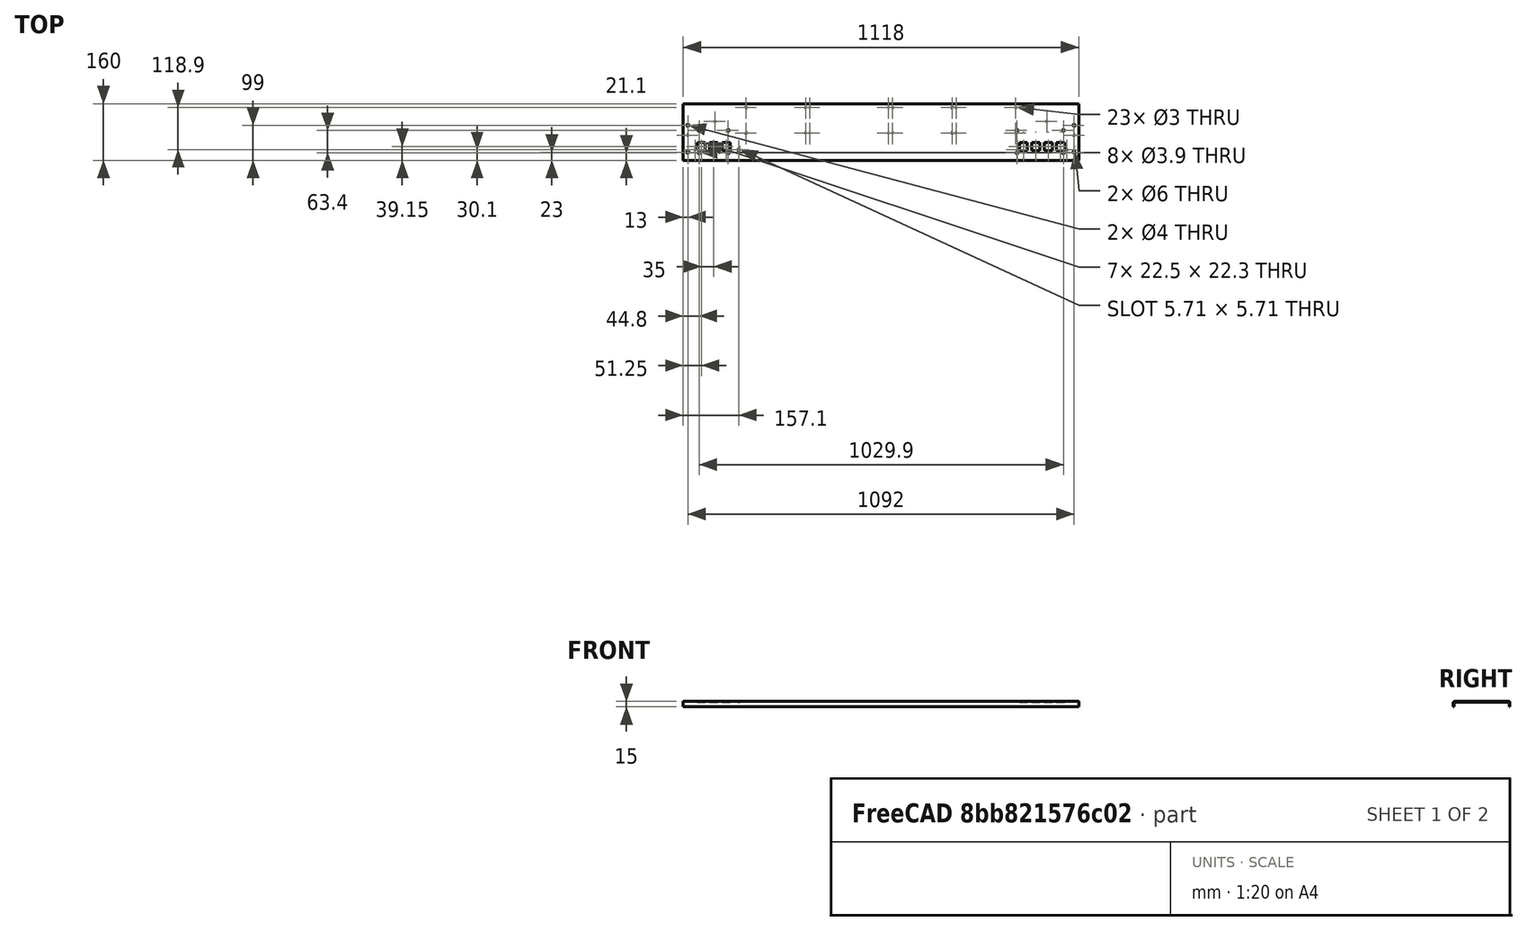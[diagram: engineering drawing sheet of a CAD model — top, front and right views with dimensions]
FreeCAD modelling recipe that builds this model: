
FCSTD DOCUMENT  (FreeCAD 0.20R29603 (Git))
Label: PanneauCommandeSupportTirettes
License: All rights reserved
LicenseURL: http://en.wikipedia.org/wiki/All_rights_reserved
objects: TechDraw::DrawViewDimension×108, TechDraw::DrawViewBalloon×27, Sketcher::SketchObject×10, TechDraw::DrawSVGTemplate×8, TechDraw::DrawViewPart×8, TechDraw::DrawPage×8, PartDesign::Pocket×7, TechDraw::DrawViewAnnotation×7, TechDraw::DrawRichAnno×5, TechDraw::DrawProjGroupItem×3, PartDesign::LinearPattern×2, PartDesign::FeaturePython×2, PartDesign::Hole×2, PartDesign::Pad×1, TechDraw::DrawProjGroup×1, PartDesign::Body×1
note: 35 computed .brp shape members not serialized (recipe doc carries the construction recipe); baked Part::Feature solids carry a one-line shape summary decoded from their .brp

FEATURE [Sketcher::SketchObject] Sketch
  FullyConstrained = true
  MapMode = 5
  Support = -> [XY_Plane]
  sketch-geometry (4):
    g0: LineSegment StartX=0 StartY=0 StartZ=0 EndX=1118 EndY=0 EndZ=0
    g1: LineSegment StartX=1118 StartY=0 StartZ=0 EndX=1118 EndY=154 EndZ=0
    g2: LineSegment StartX=1118 StartY=154 StartZ=0 EndX=0 EndY=154 EndZ=0
    g3: LineSegment StartX=0 StartY=154 StartZ=0 EndX=0 EndY=0 EndZ=0
  constraints (11):
    c: Coincident(g0,g1)
    c: Coincident(g1,g2)
    c: Coincident(g2,g3)
    c: Coincident(g3,g0)
    c: Horizontal(g0)
    c: Horizontal(g2)
    c: Vertical(g1)
    c: Vertical(g3)
    c: Coincident(g0,g-1)
    c: DistanceX(g2,g2) = 1118
    c: DistanceY(g3,g3) = 154
FEATURE [PartDesign::Pad] Pad
  Direction = (0,0,1)
  Length = 2
  Length2 = 10
  Profile = -> Sketch
  ReferenceAxis = -> Sketch [N_Axis]
  Reversed = true
  Type = 0
FEATURE [Sketcher::SketchObject] Sketch001  label="PercageGauche"
  FullyConstrained = true
  MapMode = 5
  Support = -> [XY_Plane]
  sketch-geometry (4):
    g0: LineSegment StartX=40 StartY=47.3 StartZ=0 EndX=62.5 EndY=47.3 EndZ=0
    g1: LineSegment StartX=62.5 StartY=47.3 StartZ=0 EndX=62.5 EndY=25 EndZ=0
    g2: LineSegment StartX=62.5 StartY=25 StartZ=0 EndX=40 EndY=25 EndZ=0
    g3: LineSegment StartX=40 StartY=25 StartZ=0 EndX=40 EndY=47.3 EndZ=0
  constraints (12):
    c: Coincident(g0,g1)
    c: Coincident(g1,g2)
    c: Coincident(g2,g3)
    c: Coincident(g3,g0)
    c: Horizontal(g0)
    c: Horizontal(g2)
    c: Vertical(g1)
    c: Vertical(g3)
    c: DistanceX(g2,g2) = 22.5
    c: DistanceY(g1,g1) = 22.3
    c: DistanceX(g-1,g0) = 40
    c: DistanceY(g-1,g2) = 25
FEATURE [PartDesign::Pocket] Pocket  label="PercageGauche001"
  BaseFeature = -> Pad
  Direction = (0,0,-1)
  Length = 5
  Length2 = 5
  Profile = -> Sketch001
  ReferenceAxis = -> Sketch001 [N_Axis]
  Type = 1
FEATURE [PartDesign::LinearPattern] LinearPattern
  BaseFeature = -> Pocket
  Direction = -> Sketch001 [H_Axis]
  Length = 70
  Occurrences = 3
  Originals = -> [Pocket]
FEATURE [Sketcher::SketchObject] Sketch002  label="PercageDroite"
  ExternalGeometry = -> [LinearPattern]
  FullyConstrained = true
  MapMode = 5
  Support = -> [XY_Plane]
  sketch-geometry (4):
    g0: LineSegment StartX=1055.5 StartY=47.3 StartZ=0 EndX=1078 EndY=47.3 EndZ=0
    g1: LineSegment StartX=1078 StartY=47.3 StartZ=0 EndX=1078 EndY=25 EndZ=0
    g2: LineSegment StartX=1078 StartY=25 StartZ=0 EndX=1055.5 EndY=25 EndZ=0
    g3: LineSegment StartX=1055.5 StartY=25 StartZ=0 EndX=1055.5 EndY=47.3 EndZ=0
  constraints (12):
    c: Coincident(g0,g1)
    c: Coincident(g1,g2)
    c: Coincident(g2,g3)
    c: Coincident(g3,g0)
    c: Horizontal(g0)
    c: Horizontal(g2)
    c: Vertical(g1)
    c: Vertical(g3)
    c: DistanceY(g1,g1) = 22.3
    c: DistanceX(g0,g0) = 22.5
    c: DistanceY(g-1,g2) = 25
    c: DistanceX(g-3,g1) = -40
FEATURE [PartDesign::Pocket] Pocket001  label="PercageDroite001"
  BaseFeature = -> LinearPattern
  Direction = (0,0,-1)
  Length = 5
  Length2 = 5
  Profile = -> Sketch002
  ReferenceAxis = -> Sketch002 [N_Axis]
  Type = 1
FEATURE [PartDesign::LinearPattern] LinearPattern001
  BaseFeature = -> Pocket001
  Direction = -> Sketch002 [H_Axis]
  Length = 105
  Occurrences = 4
  Originals = -> [Pocket001]
  Reversed = true
FEATURE [PartDesign::FeaturePython] Bend  # WARN: FeaturePython — macro-defined, semantics opaque (R4)
  AutoMiter = true
  BaseFeature = -> LinearPattern001
  BendType = 0
  LengthList = [12]
  LengthSpec = 0
  ReliefFactor = 0.7
  UseReliefFactor = false
  angle = 90
  baseObject = -> LinearPattern001 [Face1]
  bendAList = [90]
  extend1 = 0
  extend2 = 0
  gap1 = 0
  gap2 = 0
  invert = false
  kfactor = 0.5
  length = 12
  maxExtendDist = 5
  minGap = 0.1
  minReliefGap = 1
  miterangle1 = 0
  miterangle2 = 0
  offset = 0
  radius = 1
  reliefType = 0
  reliefd = 1
  reliefw = 0.8
  sketchflip = false
  sketchinvert = false
  unfold = false
FEATURE [PartDesign::FeaturePython] Bend001  # WARN: FeaturePython — macro-defined, semantics opaque (R4)
  AutoMiter = true
  BaseFeature = -> Bend
  BendType = 0
  LengthList = [12]
  LengthSpec = 0
  ReliefFactor = 0.7
  UseReliefFactor = false
  angle = 90
  baseObject = -> Bend [Face13]
  bendAList = [90]
  extend1 = 0
  extend2 = 0
  gap1 = 0
  gap2 = 0
  invert = false
  kfactor = 0.5
  length = 12
  maxExtendDist = 5
  minGap = 0.1
  minReliefGap = 1
  miterangle1 = 0
  miterangle2 = 0
  offset = 0
  radius = 1
  reliefType = 0
  reliefd = 1
  reliefw = 0.8
  sketchflip = false
  sketchinvert = false
  unfold = false
FEATURE [TechDraw::DrawSVGTemplate] Template
  Height = 210
  Orientation = 1
  Width = 297
FEATURE [TechDraw::DrawProjGroupItem] ProjItem  label="Front"
  CoarseView = false
  Direction = (0,0,1)
  Focus = 100
  HardHidden = false
  IsoCount = 0
  IsoHidden = false
  IsoVisible = false
  LockPosition = true
  Perspective = false
  Rotation = 0
  RotationVector = (1,0,0)
  Scale = 0.2
  ScaleType = 2
  SeamHidden = false
  SeamVisible = true
  SmoothHidden = false
  SmoothVisible = true
  Source = -> [Bend001]
  Type = 0
  X = 0
  XDirection = (1,0,0)
  Y = 0
FEATURE [TechDraw::DrawProjGroupItem] ProjItem001  label="Bottom"
  CoarseView = false
  Direction = (0,-1,0)
  Focus = 100
  HardHidden = false
  IsoCount = 0
  IsoHidden = false
  IsoVisible = false
  LockPosition = false
  Perspective = false
  Rotation = 0
  RotationVector = (1,0,0)
  ScaleType = 2
  SeamHidden = false
  SeamVisible = true
  SmoothHidden = false
  SmoothVisible = true
  Source = -> [Bend001]
  Type = 5
  X = 0
  XDirection = (1,0,0)
  Y = 47
FEATURE [TechDraw::DrawProjGroupItem] ProjItem002  label="Right"
  CoarseView = false
  Direction = (1,0,1e-16)
  Focus = 100
  HardHidden = false
  IsoCount = 0
  IsoHidden = false
  IsoVisible = false
  LockPosition = false
  Perspective = false
  Rotation = 0
  RotationVector = (1,0,0)
  ScaleType = 2
  SeamHidden = false
  SeamVisible = true
  SmoothHidden = false
  SmoothVisible = true
  Source = -> [Bend001]
  Type = 2
  X = -152.058
  XDirection = (1e-16,0,-1)
  Y = 0
FEATURE [TechDraw::DrawProjGroup] ProjGroup
  Anchor = -> ProjItem
  AutoDistribute = false
  LockPosition = false
  ProjectionType = 0
  Rotation = 0
  Scale = 0.2
  ScaleType = 2
  Source = -> [Bend001]
  Views = -> [ProjItem,ProjItem001,ProjItem002]
  X = 172.705
  Y = 99.0316
  spacingX = 15
  spacingY = 15
FEATURE [TechDraw::DrawViewDimension] Dimension
  AngleOverride = false
  Arbitrary = false
  ArbitraryTolerances = false
  EqualTolerance = true
  ExtensionAngle = 0
  FormatSpec = %.2w
  FormatSpecOverTolerance = %+.2w
  FormatSpecUnderTolerance = %+.2w
  Inverted = false
  LineAngle = 0
  LockPosition = false
  MeasureType = 1
  OverTolerance = 0
  References2D = -> [ProjItem]
  Rotation = 0
  ScaleType = 0
  TheoreticalExact = false
  Type = 1
  UnderTolerance = 0
  X = 2.98421
  Y = -48.3158
FEATURE [TechDraw::DrawViewDimension] Dimension001
  AngleOverride = false
  Arbitrary = false
  ArbitraryTolerances = false
  EqualTolerance = true
  ExtensionAngle = 0
  FormatSpec = %.2w
  FormatSpecOverTolerance = %+.2w
  FormatSpecUnderTolerance = %+.2w
  Inverted = false
  LineAngle = 0
  LockPosition = false
  MeasureType = 1
  OverTolerance = 0
  References2D = -> [ProjItem]
  Rotation = 0
  ScaleType = 0
  TheoreticalExact = false
  Type = 2
  UnderTolerance = 0
  X = -126.143
  Y = 3.14776
FEATURE [TechDraw::DrawViewBalloon] Balloon
  BubbleShape = 0
  EndType = 0
  EndTypeScale = 1
  KinkLength = 5
  LockPosition = false
  OriginX = -215.581
  OriginY = -7.47892
  Rotation = 0
  ScaleType = 0
  ShapeScale = 1
  SourceView = -> ProjItem
  Text = 1
  TextWrapLen = -1
  X = -91.4035
  Y = 121.304
FEATURE [TechDraw::DrawViewBalloon] Balloon001
  BubbleShape = 0
  EndType = 0
  EndTypeScale = 1
  KinkLength = 5
  LockPosition = false
  OriginX = -5.49057
  OriginY = 0
  Rotation = 0
  ScaleType = 0
  ShapeScale = 1
  SourceView = -> ProjItem002
  Text = 2
  TextWrapLen = -1
  X = 94.5094
  Y = 100
FEATURE [TechDraw::DrawRichAnno] RichTextAnnotation
  AnnoText = <!DOCTYPE HTML PUBLIC "-//W3C//DTD HTML 4.0//EN" "http://www.w3.org/TR/REC-html40/strict.dtd">\n<html><head><meta name="qrichtext" content="1" /><style type="text/css">\np, li { white-space: pre-wrap; }\n</style></head><body style=" font-family:'osifont'; font-size:9pt; font-weight:400; font-style:normal;">\n<p style=" margin-top:0px; margin-bottom:0px; margin-left:0px; margin-right:0px; -qt-block-indent:0; text-indent:0px;"><span style=" font-family:'Sans Serif'; font-size:10pt;">1 : vue de dessus</span></p>\n<p style=" margin-top:0px; margin-bottom:0px; margin-left:0px; margin-right:0px; -qt-block-indent:0; text-indent:0px;"><span style=" font-family:'Sans Serif'; font-size:10pt;">2 : dessous de la pièce</span></p></body></html>
  LockPosition = false
  MaxWidth = -1
  Rotation = 0
  ScaleType = 0
  ShowFrame = false
  X = 55.4737
  Y = 20.7237
FEATURE [TechDraw::DrawSVGTemplate] Template001
  Height = 210
  Orientation = 1
  Width = 297
FEATURE [TechDraw::DrawViewPart] View001
  CoarseView = false
  Direction = (1,0,0)
  Focus = 100
  HardHidden = false
  IsoCount = 0
  IsoHidden = false
  IsoVisible = false
  LockPosition = false
  Perspective = false
  Rotation = 90
  ScaleType = 2
  SeamHidden = false
  SeamVisible = true
  SmoothHidden = false
  SmoothVisible = true
  Source = -> [Bend001]
  X = 148.5
  XDirection = (1,0,0)
  Y = 105
FEATURE [TechDraw::DrawViewDimension] Dimension002
  AngleOverride = false
  Arbitrary = false
  ArbitraryTolerances = false
  EqualTolerance = true
  ExtensionAngle = 0
  FormatSpec = %.2w
  FormatSpecOverTolerance = %+.2w
  FormatSpecUnderTolerance = %+.2w
  Inverted = false
  LineAngle = 0
  LockPosition = false
  MeasureType = 1
  OverTolerance = 0
  References2D = -> [View001]
  Rotation = 0
  ScaleType = 0
  TheoreticalExact = false
  Type = 1
  UnderTolerance = 0
  X = 0.257011
  Y = 40.0608
FEATURE [TechDraw::DrawViewDimension] Dimension003
  AngleOverride = false
  Arbitrary = false
  ArbitraryTolerances = false
  EqualTolerance = true
  ExtensionAngle = 0
  FormatSpec = %.2w
  FormatSpecOverTolerance = %+.2w
  FormatSpecUnderTolerance = %+.2w
  Inverted = false
  LineAngle = 0
  LockPosition = false
  MeasureType = 1
  OverTolerance = 0
  References2D = -> [View001]
  Rotation = 0
  ScaleType = 0
  TheoreticalExact = false
  Type = 1
  UnderTolerance = 0
  X = -0.514022
  Y = 59.6778
FEATURE [TechDraw::DrawViewDimension] Dimension004
  AngleOverride = false
  Arbitrary = false
  ArbitraryTolerances = false
  EqualTolerance = true
  ExtensionAngle = 0
  FormatSpec = %.2w
  FormatSpecOverTolerance = %+.2w
  FormatSpecUnderTolerance = %+.2w
  Inverted = false
  LineAngle = 0
  LockPosition = false
  MeasureType = 1
  OverTolerance = 0
  References2D = -> [View001]
  Rotation = 0
  ScaleType = 0
  TheoreticalExact = false
  Type = 2
  UnderTolerance = 0
  X = -112.168
  Y = -14.9862
FEATURE [TechDraw::DrawViewBalloon] Balloon002
  BubbleShape = 0
  EndType = 0
  EndTypeScale = 1
  KinkLength = 5
  LockPosition = false
  OriginX = -2.27e-14
  OriginY = 5.49057
  Rotation = 0
  ScaleType = 0
  ShapeScale = 1
  SourceView = -> View001
  Text = 1
  TextWrapLen = -1
  X = 25
  Y = -25
FEATURE [TechDraw::DrawRichAnno] RichTextAnnotation001
  AnnoText = <!DOCTYPE HTML PUBLIC "-//W3C//DTD HTML 4.0//EN" "http://www.w3.org/TR/REC-html40/strict.dtd">\n<html><head><meta name="qrichtext" content="1" /><style type="text/css">\np, li { white-space: pre-wrap; }\n</style></head><body style=" font-family:'Sans Serif'; font-size:9pt; font-weight:400; font-style:normal;">\n<p style=" margin-top:0px; margin-bottom:0px; margin-left:0px; margin-right:0px; -qt-block-indent:0; text-indent:0px;"><span style=" font-size:10pt;">1 : dessous de la pièce</span></p></body></html>
  LockPosition = false
  MaxWidth = -1
  Rotation = 0
  ScaleType = 0
  ShowFrame = false
  X = 91.5
  Y = 44
FEATURE [TechDraw::DrawViewDimension] Dimension005
  AngleOverride = false
  Arbitrary = false
  ArbitraryTolerances = false
  EqualTolerance = true
  ExtensionAngle = 0
  FormatSpec = %.2w
  FormatSpecOverTolerance = %+.2w
  FormatSpecUnderTolerance = %+.2w
  Inverted = false
  LineAngle = 0
  LockPosition = false
  MeasureType = 1
  OverTolerance = 0
  References2D = -> [View001]
  Rotation = 0
  ScaleType = 0
  TheoreticalExact = false
  Type = 2
  UnderTolerance = 0
  X = 99.7898
  Y = -15.7151
FEATURE [TechDraw::DrawPage] Page001  label="vue-de-cote"
  KeepUpdated = true
  NextBalloonIndex = 2
  ProjectionType = 0
  Template = -> Template001
  Views = -> [View001,Dimension002,Dimension003,Dimension004,Balloon002,RichTextAnnotation001,Dimension005]
FEATURE [TechDraw::DrawSVGTemplate] Template002
  Height = 210
  Orientation = 1
  Width = 297
FEATURE [TechDraw::DrawViewPart] View
  CoarseView = false
  Direction = (0,0,1)
  Focus = 100
  HardHidden = false
  IsoCount = 0
  IsoHidden = false
  IsoVisible = false
  LockPosition = false
  Perspective = false
  Rotation = 0
  Scale = 0.5
  ScaleType = 2
  SeamHidden = false
  SeamVisible = true
  SmoothHidden = false
  SmoothVisible = false
  Source = -> [Bend001]
  X = 301.855
  XDirection = (1,0,0)
  Y = 156.671
FEATURE [TechDraw::DrawViewPart] View002
  CoarseView = false
  Direction = (0,0,1)
  Focus = 100
  HardHidden = false
  IsoCount = 0
  IsoHidden = false
  IsoVisible = false
  LockPosition = false
  Perspective = false
  Rotation = 0
  Scale = 0.5
  ScaleType = 2
  SeamHidden = false
  SeamVisible = true
  SmoothHidden = false
  SmoothVisible = false
  Source = -> [Bend001]
  X = -2.92105
  XDirection = (1,0,0)
  Y = 57.4737
FEATURE [TechDraw::DrawViewDimension] Dimension006
  AngleOverride = false
  Arbitrary = false
  ArbitraryTolerances = false
  EqualTolerance = true
  ExtensionAngle = 0
  FormatSpec = %.2w
  FormatSpecOverTolerance = %+.2w
  FormatSpecUnderTolerance = %+.2w
  Inverted = false
  LineAngle = 0
  LockPosition = false
  MeasureType = 1
  OverTolerance = 0
  References2D = -> [View]
  Rotation = 0
  ScaleType = 0
  TheoreticalExact = false
  Type = 1
  UnderTolerance = 0
  X = -268.36
  Y = 20.4992
FEATURE [TechDraw::DrawViewDimension] Dimension007
  AngleOverride = false
  Arbitrary = false
  ArbitraryTolerances = false
  EqualTolerance = true
  ExtensionAngle = 0
  FormatSpec = %.2w
  FormatSpecOverTolerance = %+.2w
  FormatSpecUnderTolerance = %+.2w
  Inverted = false
  LineAngle = 0
  LockPosition = false
  MeasureType = 1
  OverTolerance = 0
  References2D = -> [View]
  Rotation = 0
  ScaleType = 0
  TheoreticalExact = false
  Type = 1
  UnderTolerance = 0
  X = -236.467
  Y = 34.6237
FEATURE [TechDraw::DrawViewDimension] Dimension008
  AngleOverride = false
  Arbitrary = false
  ArbitraryTolerances = false
  EqualTolerance = true
  ExtensionAngle = 0
  FormatSpec = %.2w
  FormatSpecOverTolerance = %+.2w
  FormatSpecUnderTolerance = %+.2w
  Inverted = false
  LineAngle = 0
  LockPosition = false
  MeasureType = 1
  OverTolerance = 0
  References2D = -> [View]
  Rotation = 0
  ScaleType = 0
  TheoreticalExact = false
  Type = 1
  UnderTolerance = 0
  X = -217.586
  Y = 24.6763
FEATURE [TechDraw::DrawViewDimension] Dimension009
  AngleOverride = false
  Arbitrary = false
  ArbitraryTolerances = false
  EqualTolerance = true
  ExtensionAngle = 0
  FormatSpec = %.2w
  FormatSpecOverTolerance = %+.2w
  FormatSpecUnderTolerance = %+.2w
  Inverted = false
  LineAngle = 0
  LockPosition = false
  MeasureType = 1
  OverTolerance = 0
  References2D = -> [View]
  Rotation = 0
  ScaleType = 0
  TheoreticalExact = false
  Type = 1
  UnderTolerance = 0
  X = -199.257
  Y = 14.4526
FEATURE [TechDraw::DrawViewDimension] Dimension010
  AngleOverride = false
  Arbitrary = false
  ArbitraryTolerances = false
  EqualTolerance = true
  ExtensionAngle = 0
  FormatSpec = %.2w
  FormatSpecOverTolerance = %+.2w
  FormatSpecUnderTolerance = %+.2w
  Inverted = false
  LineAngle = 0
  LockPosition = false
  MeasureType = 1
  OverTolerance = 0
  References2D = -> [View]
  Rotation = 0
  ScaleType = 0
  TheoreticalExact = false
  Type = 2
  UnderTolerance = 0
  X = -185.066
  Y = 0.864474
FEATURE [TechDraw::DrawViewDimension] Dimension011
  AngleOverride = false
  Arbitrary = false
  ArbitraryTolerances = false
  EqualTolerance = true
  ExtensionAngle = 0
  FormatSpec = %.2w
  FormatSpecOverTolerance = %+.2w
  FormatSpecUnderTolerance = %+.2w
  Inverted = false
  LineAngle = 0
  LockPosition = false
  MeasureType = 1
  OverTolerance = 0
  References2D = -> [View]
  Rotation = 0
  ScaleType = 0
  TheoreticalExact = false
  Type = 2
  UnderTolerance = 0
  X = -168.395
  Y = -11.7895
FEATURE [TechDraw::DrawViewDimension] Dimension012
  AngleOverride = false
  Arbitrary = false
  ArbitraryTolerances = false
  EqualTolerance = true
  ExtensionAngle = 0
  FormatSpec = %.2w
  FormatSpecOverTolerance = %+.2w
  FormatSpecUnderTolerance = %+.2w
  Inverted = false
  LineAngle = 0
  LockPosition = false
  MeasureType = 1
  OverTolerance = 0
  References2D = -> [View]
  Rotation = 0
  ScaleType = 0
  TheoreticalExact = false
  Type = 2
  UnderTolerance = 0
  X = -152.737
  Y = -11.4342
FEATURE [TechDraw::DrawViewDimension] Dimension013
  AngleOverride = false
  Arbitrary = false
  ArbitraryTolerances = false
  EqualTolerance = true
  ExtensionAngle = 0
  FormatSpec = %.2w
  FormatSpecOverTolerance = %+.2w
  FormatSpecUnderTolerance = %+.2w
  Inverted = false
  LineAngle = 0
  LockPosition = false
  MeasureType = 1
  OverTolerance = 0
  References2D = -> [View]
  Rotation = 0
  ScaleType = 0
  TheoreticalExact = false
  Type = 1
  UnderTolerance = 0
  X = -267.714
  Y = -3.02507
FEATURE [TechDraw::DrawViewDimension] Dimension014
  AngleOverride = false
  Arbitrary = false
  ArbitraryTolerances = false
  EqualTolerance = true
  ExtensionAngle = 0
  FormatSpec = %.2w
  FormatSpecOverTolerance = %+.2w
  FormatSpecUnderTolerance = %+.2w
  Inverted = false
  LineAngle = 0
  LockPosition = false
  MeasureType = 1
  OverTolerance = 0
  References2D = -> [View]
  Rotation = 0
  ScaleType = 0
  TheoreticalExact = false
  Type = 1
  UnderTolerance = 0
  X = -203.309
  Y = 3.67632
FEATURE [TechDraw::DrawViewDimension] Dimension015
  AngleOverride = false
  Arbitrary = false
  ArbitraryTolerances = false
  EqualTolerance = true
  ExtensionAngle = 0
  FormatSpec = %.2w
  FormatSpecOverTolerance = %+.2w
  FormatSpecUnderTolerance = %+.2w
  Inverted = false
  LineAngle = 0
  LockPosition = false
  MeasureType = 1
  OverTolerance = 0
  References2D = -> [View002]
  Rotation = 0
  ScaleType = 0
  TheoreticalExact = false
  Type = 1
  UnderTolerance = 0
  X = 269.224
  Y = 8.37368
FEATURE [TechDraw::DrawViewDimension] Dimension016
  AngleOverride = false
  Arbitrary = false
  ArbitraryTolerances = false
  EqualTolerance = true
  ExtensionAngle = 0
  FormatSpec = %.2w
  FormatSpecOverTolerance = %+.2w
  FormatSpecUnderTolerance = %+.2w
  Inverted = false
  LineAngle = 0
  LockPosition = false
  MeasureType = 1
  OverTolerance = 0
  References2D = -> [View002]
  Rotation = 0
  ScaleType = 0
  TheoreticalExact = false
  Type = 2
  UnderTolerance = 0
  X = 264.75
  Y = -16.6934
FEATURE [TechDraw::DrawViewDimension] Dimension017
  AngleOverride = false
  Arbitrary = false
  ArbitraryTolerances = false
  EqualTolerance = true
  ExtensionAngle = 0
  FormatSpec = %.2w
  FormatSpecOverTolerance = %+.2w
  FormatSpecUnderTolerance = %+.2w
  Inverted = false
  LineAngle = 0
  LockPosition = false
  MeasureType = 1
  OverTolerance = 0
  References2D = -> [View002]
  Rotation = 0
  ScaleType = 0
  TheoreticalExact = false
  Type = 2
  UnderTolerance = 0
  X = 273.03
  Y = -16.9251
FEATURE [TechDraw::DrawViewDimension] Dimension018
  AngleOverride = false
  Arbitrary = false
  ArbitraryTolerances = false
  EqualTolerance = true
  ExtensionAngle = 0
  FormatSpec = %.2w
  FormatSpecOverTolerance = %+.2w
  FormatSpecUnderTolerance = %+.2w
  Inverted = false
  LineAngle = 0
  LockPosition = false
  MeasureType = 1
  OverTolerance = 0
  References2D = -> [View002]
  Rotation = 0
  ScaleType = 0
  TheoreticalExact = false
  Type = 1
  UnderTolerance = 0
  X = 185.217
  Y = 0.390089
FEATURE [TechDraw::DrawViewDimension] Dimension019
  AngleOverride = false
  Arbitrary = false
  ArbitraryTolerances = false
  EqualTolerance = true
  ExtensionAngle = 0
  FormatSpec = %.2w
  FormatSpecOverTolerance = %+.2w
  FormatSpecUnderTolerance = %+.2w
  Inverted = false
  LineAngle = 0
  LockPosition = false
  MeasureType = 1
  OverTolerance = 0
  References2D = -> [View002]
  Rotation = 0
  ScaleType = 0
  TheoreticalExact = false
  Type = 1
  UnderTolerance = 0
  X = 201.785
  Y = 9.40137
FEATURE [TechDraw::DrawViewDimension] Dimension020
  AngleOverride = false
  Arbitrary = false
  ArbitraryTolerances = false
  EqualTolerance = true
  ExtensionAngle = 0
  FormatSpec = %.2w
  FormatSpecOverTolerance = %+.2w
  FormatSpecUnderTolerance = %+.2w
  Inverted = false
  LineAngle = 0
  LockPosition = false
  MeasureType = 1
  OverTolerance = 0
  References2D = -> [View002]
  Rotation = 0
  ScaleType = 0
  TheoreticalExact = false
  Type = 1
  UnderTolerance = 0
  X = 218.352
  Y = 19.6556
FEATURE [TechDraw::DrawViewDimension] Dimension021
  AngleOverride = false
  Arbitrary = false
  ArbitraryTolerances = false
  EqualTolerance = true
  ExtensionAngle = 0
  FormatSpec = %.2w
  FormatSpecOverTolerance = %+.2w
  FormatSpecUnderTolerance = %+.2w
  Inverted = false
  LineAngle = 0
  LockPosition = false
  MeasureType = 1
  OverTolerance = 0
  References2D = -> [View002]
  Rotation = 0
  ScaleType = 0
  TheoreticalExact = false
  Type = 1
  UnderTolerance = 0
  X = 236.163
  Y = 28.6669
FEATURE [TechDraw::DrawViewDimension] Dimension022
  AngleOverride = false
  Arbitrary = false
  ArbitraryTolerances = false
  EqualTolerance = true
  ExtensionAngle = 0
  FormatSpec = %.2w
  FormatSpecOverTolerance = %+.2w
  FormatSpecUnderTolerance = %+.2w
  Inverted = false
  LineAngle = 0
  LockPosition = false
  MeasureType = 1
  OverTolerance = 0
  References2D = -> [View002]
  Rotation = 0
  ScaleType = 0
  TheoreticalExact = false
  Type = 2
  UnderTolerance = 0
  X = 166.541
  Y = 2.58344
FEATURE [TechDraw::DrawViewDimension] Dimension023
  AngleOverride = false
  Arbitrary = false
  ArbitraryTolerances = false
  EqualTolerance = true
  ExtensionAngle = 0
  FormatSpec = %.2w
  FormatSpecOverTolerance = %+.2w
  FormatSpecUnderTolerance = %+.2w
  Inverted = false
  LineAngle = 0
  LockPosition = false
  MeasureType = 1
  OverTolerance = 0
  References2D = -> [View002]
  Rotation = 0
  ScaleType = 0
  TheoreticalExact = false
  Type = 1
  UnderTolerance = 0
  X = 198.317
  Y = -30.0618
FEATURE [TechDraw::DrawViewDimension] Dimension024
  AngleOverride = false
  Arbitrary = false
  ArbitraryTolerances = false
  EqualTolerance = true
  ExtensionAngle = 0
  FormatSpec = %.2w
  FormatSpecOverTolerance = %+.2w
  FormatSpecUnderTolerance = %+.2w
  Inverted = false
  LineAngle = 0
  LockPosition = false
  MeasureType = 1
  OverTolerance = 0
  References2D = -> [View002]
  Rotation = 0
  ScaleType = 0
  TheoreticalExact = false
  Type = 1
  UnderTolerance = 0
  X = 236.326
  Y = -27.576
FEATURE [TechDraw::DrawViewDimension] Dimension025
  AngleOverride = false
  Arbitrary = false
  ArbitraryTolerances = false
  EqualTolerance = true
  ExtensionAngle = 0
  FormatSpec = %.2w
  FormatSpecOverTolerance = %+.2w
  FormatSpecUnderTolerance = %+.2w
  Inverted = false
  LineAngle = 0
  LockPosition = false
  MeasureType = 1
  OverTolerance = 0
  References2D = -> [View002]
  Rotation = 0
  ScaleType = 0
  TheoreticalExact = false
  Type = 1
  UnderTolerance = 0
  X = 259.419
  Y = -30.0618
FEATURE [TechDraw::DrawRichAnno] RichTextAnnotation002
  AnnoText = <!DOCTYPE HTML PUBLIC "-//W3C//DTD HTML 4.0//EN" "http://www.w3.org/TR/REC-html40/strict.dtd">\n<html><head><meta name="qrichtext" content="1" /><style type="text/css">\np, li { white-space: pre-wrap; }\n</style></head><body style=" font-family:'Sans Serif'; font-size:9pt; font-weight:400; font-style:normal;">\n<p style=" margin-top:0px; margin-bottom:0px; margin-left:0px; margin-right:0px; -qt-block-indent:0; text-indent:0px;"><span style=" font-size:10pt;">Perçages de droite</span></p></body></html>
  LockPosition = false
  MaxWidth = -1
  Rotation = 0
  ScaleType = 0
  ShowFrame = false
  X = 168.698
  Y = 78.2769
FEATURE [TechDraw::DrawRichAnno] RichTextAnnotation003
  AnnoText = <!DOCTYPE HTML PUBLIC "-//W3C//DTD HTML 4.0//EN" "http://www.w3.org/TR/REC-html40/strict.dtd">\n<html><head><meta name="qrichtext" content="1" /><style type="text/css">\np, li { white-space: pre-wrap; }\n</style></head><body style=" font-family:'Sans Serif'; font-size:9pt; font-weight:400; font-style:normal;">\n<p style=" margin-top:0px; margin-bottom:0px; margin-left:0px; margin-right:0px; -qt-block-indent:0; text-indent:0px;"><span style=" font-size:10pt;">Perçages de gauche</span></p></body></html>
  LockPosition = false
  MaxWidth = -1
  Rotation = 0
  ScaleType = 0
  ShowFrame = false
  X = 142.907
  Y = 174.915
FEATURE [TechDraw::DrawPage] Page002  label="vue-percages-boutons"
  KeepUpdated = true
  NextBalloonIndex = 1
  ProjectionType = 0
  Template = -> Template002
  Views = -> [View,View002,Dimension006,Dimension007,Dimension008,Dimension009,Dimension010,Dimension011,Dimension012,Dimension013,Dimension014,Dimension015,Dimension016,Dimension017,Dimension018,Dimension019,Dimension020,Dimension021,Dimension022,Dimension023,Dimension024,Dimension025,RichTextAnnotation002,RichTextAnnotation003]
FEATURE [TechDraw::DrawRichAnno] RichTextAnnotation004
  AnnoText = <!DOCTYPE HTML PUBLIC "-//W3C//DTD HTML 4.0//EN" "http://www.w3.org/TR/REC-html40/strict.dtd">\n<html><head><meta name="qrichtext" content="1" /><style type="text/css">\np, li { white-space: pre-wrap; }\n</style></head><body style=" font-family:'Sans Serif'; font-size:9pt; font-weight:400; font-style:normal;">\n<p style=" margin-top:0px; margin-bottom:0px; margin-left:0px; margin-right:0px; -qt-block-indent:0; text-indent:0px;"><span style=" font-size:10pt;">Acier épaisseur 2mm</span></p></body></html>
  LockPosition = false
  MaxWidth = -1
  Rotation = 0
  ScaleType = 0
  ShowFrame = false
  X = 167.013
  Y = 178.224
FEATURE [TechDraw::DrawPage] Page  label="vue-generale"
  KeepUpdated = true
  NextBalloonIndex = 3
  ProjectionType = 0
  Template = -> Template
  Views = -> [ProjGroup,Dimension,Dimension001,Balloon,Balloon001,RichTextAnnotation,RichTextAnnotation004]
FEATURE [Sketcher::SketchObject] Sketch003  label="Sketch Trous fixation cartes VC et Perc."
  ExternalGeometry = -> [Bend001]
  FullyConstrained = true
  MapMode = 5
  Support = -> [Bend001]
  sketch-geometry (8):
    g0: Circle CenterX=44.8 CenterY=81.5 CenterZ=0 NormalX=0 NormalY=0 NormalZ=1 AngleXU=0 Radius=1.75
    g1: Circle CenterX=127.2 CenterY=81.5 CenterZ=0 NormalX=0 NormalY=0 NormalZ=1 AngleXU=0 Radius=1.75
    g2: Circle CenterX=44.8 CenterY=18.1 CenterZ=0 NormalX=0 NormalY=0 NormalZ=1 AngleXU=0 Radius=1.75
    g3: Circle CenterX=127.2 CenterY=18.1 CenterZ=0 NormalX=0 NormalY=0 NormalZ=1 AngleXU=0 Radius=1.75
    g4: Circle CenterX=943.5 CenterY=81.5 CenterZ=0 NormalX=0 NormalY=0 NormalZ=1 AngleXU=0 Radius=1.75
    g5: Circle CenterX=1074.7 CenterY=81.5 CenterZ=0 NormalX=0 NormalY=0 NormalZ=1 AngleXU=0 Radius=1.75
    g6: Circle CenterX=943.5 CenterY=18.1 CenterZ=0 NormalX=0 NormalY=0 NormalZ=1 AngleXU=0 Radius=1.75
    g7: Circle CenterX=1074.7 CenterY=18.1 CenterZ=0 NormalX=0 NormalY=0 NormalZ=1 AngleXU=0 Radius=1.75
  constraints (24):
    c: Horizontal(g0,g1)
    c: Horizontal(g2,g3)
    c: Vertical(g0,g2)
    c: Vertical(g1,g3)
    c: Diameter(g0) = 3.5
    c: Diameter(g1) = 3.5
    c: Diameter(g3) = 3.5
    c: Diameter(g2) = 3.5
    c: DistanceX(g0,g1) = 82.4
    c: DistanceY(g3,g1) = 63.4
    c: Diameter(g4) = 3.5
    c: Diameter(g5) = 3.5
    c: Diameter(g7) = 3.5
    c: Diameter(g6) = 3.5
    c: Vertical(g4,g6)
    c: Vertical(g5,g7)
    c: DistanceX(g4,g5) = 131.2
    c: DistanceY(g7,g5) = 63.4
    c: DistanceY(g2) = 18.1
    c: DistanceX(g2) = 44.8
    c: DistanceX(g7,g-3) = 43.3
    c: Horizontal(g6,g7)
    c: Horizontal(g4,g5)
    c: Horizontal(g6,g3)
FEATURE [PartDesign::Hole] Hole  label="Trous fixation cartes VC et Perc."
  BaseFeature = -> Bend001
  CustomThreadClearance = 0
  Depth = 2281.57
  DepthType = 1
  Diameter = 3.9
  DrillForDepth = false
  DrillPoint = 1
  DrillPointAngle = 118
  HoleCutCountersinkAngle = 90
  HoleCutCustomValues = false
  HoleCutDepth = 0
  HoleCutDiameter = 6.1
  HoleCutType = 2
  ModelThread = false
  Profile = -> Sketch003
  Tapered = false
  TaperedAngle = 90
  ThreadClass = 0
  ThreadDepth = 2281.57
  ThreadDepthType = 0
  ThreadDirection = 0
  ThreadFit = 0
  ThreadSize = 10
  ThreadType = 1
  Threaded = false
  UseCustomThreadClearance = false
FEATURE [Sketcher::SketchObject] Sketch004  label="Sketch trous fixation entretoise simple"
  ExternalGeometry = -> [Hole]
  FullyConstrained = true
  MapMode = 5
  Support = -> [Hole]
  sketch-geometry (4):
    g0: Circle CenterX=177.9 CenterY=146 CenterZ=0 NormalX=0 NormalY=0 NormalZ=1 AngleXU=0 Radius=1.5
    g1: Circle CenterX=177.9 CenterY=74.3 CenterZ=0 NormalX=0 NormalY=0 NormalZ=1 AngleXU=0 Radius=1.5
    g2: Circle CenterX=939.7 CenterY=146 CenterZ=0 NormalX=0 NormalY=0 NormalZ=1 AngleXU=0 Radius=1.5
    g3: Circle CenterX=939.7 CenterY=74.3 CenterZ=0 NormalX=0 NormalY=0 NormalZ=1 AngleXU=0 Radius=1.5
  constraints (12):
    c: Vertical(g1,g0)
    c: DistanceY(g1,g0) = 71.7
    c: Diameter(g0) = 3
    c: Diameter(g1) = 3
    c: DistanceX(g0) = 177.9
    c: DistanceY(g1) = 74.3
    c: Vertical(g3,g2)
    c: DistanceY(g3,g2) = 71.7
    c: Equal(g0,g2) = 3
    c: Equal(g1,g3) = 3
    c: Horizontal(g3,g1)
    c: DistanceX(g2,g-3) = 178.3
FEATURE [PartDesign::Pocket] Pocket002  label="Trous fixation entretoise simple"
  BaseFeature = -> Hole
  Direction = (0,0,-1)
  Length = 5
  Length2 = 5
  Profile = -> Sketch004
  ReferenceAxis = -> Sketch004 [N_Axis]
  Type = 1
FEATURE [Sketcher::SketchObject] Sketch005  label="Sketch trous fixation entretoise double"
  ExternalGeometry = -> [Pocket002]
  FullyConstrained = true
  MapMode = 5
  Support = -> [Pocket002]
  sketch-geometry (24):
    g0: LineSegment StartX=346.1 StartY=146 StartZ=0 EndX=357.7 EndY=146 EndZ=0
    g1: LineSegment StartX=357.7 StartY=146 StartZ=0 EndX=357.7 EndY=74.3 EndZ=0
    g2: LineSegment StartX=357.7 StartY=74.3 StartZ=0 EndX=346.1 EndY=74.3 EndZ=0
    g3: LineSegment StartX=346.1 StartY=74.3 StartZ=0 EndX=346.1 EndY=146 EndZ=0
    g4: Circle CenterX=346.1 CenterY=146 CenterZ=0 NormalX=0 NormalY=0 NormalZ=1 AngleXU=0 Radius=1.5
    g5: Circle CenterX=357.7 CenterY=146 CenterZ=0 NormalX=0 NormalY=0 NormalZ=1 AngleXU=0 Radius=1.5
    g6: Circle CenterX=357.7 CenterY=74.3 CenterZ=0 NormalX=0 NormalY=0 NormalZ=1 AngleXU=0 Radius=1.5
    g7: Circle CenterX=346.1 CenterY=74.3 CenterZ=0 NormalX=0 NormalY=0 NormalZ=1 AngleXU=0 Radius=1.5
    g8: LineSegment StartX=591.7 StartY=146 StartZ=0 EndX=580.1 EndY=146 EndZ=0
    g9: LineSegment StartX=580.1 StartY=146 StartZ=0 EndX=580.1 EndY=74.3 EndZ=0
    g10: LineSegment StartX=580.1 StartY=74.3 StartZ=0 EndX=591.7 EndY=74.3 EndZ=0
    g11: LineSegment StartX=591.7 StartY=74.3 StartZ=0 EndX=591.7 EndY=146 EndZ=0
    g12: Circle CenterX=591.7 CenterY=146 CenterZ=0 NormalX=0 NormalY=0 NormalZ=1 AngleXU=0 Radius=1.5
    g13: Circle CenterX=580.1 CenterY=146 CenterZ=0 NormalX=0 NormalY=0 NormalZ=1 AngleXU=0 Radius=1.5
    g14: Circle CenterX=580.1 CenterY=74.3 CenterZ=0 NormalX=0 NormalY=0 NormalZ=1 AngleXU=0 Radius=1.5
    g15: Circle CenterX=591.7 CenterY=74.3 CenterZ=0 NormalX=0 NormalY=0 NormalZ=1 AngleXU=0 Radius=1.5
    g16: LineSegment StartX=771.5 StartY=146 StartZ=0 EndX=759.9 EndY=146 EndZ=0
    g17: LineSegment StartX=759.9 StartY=146 StartZ=0 EndX=759.9 EndY=74.3 EndZ=0
    g18: LineSegment StartX=759.9 StartY=74.3 StartZ=0 EndX=771.5 EndY=74.3 EndZ=0
    g19: LineSegment StartX=771.5 StartY=74.3 StartZ=0 EndX=771.5 EndY=146 EndZ=0
    g20: Circle CenterX=771.5 CenterY=146 CenterZ=0 NormalX=0 NormalY=0 NormalZ=1 AngleXU=0 Radius=1.5
    g21: Circle CenterX=759.9 CenterY=146 CenterZ=0 NormalX=0 NormalY=0 NormalZ=1 AngleXU=0 Radius=1.5
    g22: Circle CenterX=759.9 CenterY=74.3 CenterZ=0 NormalX=0 NormalY=0 NormalZ=1 AngleXU=0 Radius=1.5
    g23: Circle CenterX=771.5 CenterY=74.3 CenterZ=0 NormalX=0 NormalY=0 NormalZ=1 AngleXU=0 Radius=1.5
  constraints (61):
    c: Coincident(g0,g1)
    c: Coincident(g1,g2)
    c: Coincident(g2,g3)
    c: Coincident(g3,g0)
    c: Horizontal(g0)
    c: Horizontal(g2)
    c: Vertical(g1)
    c: Vertical(g3)
    c: Coincident(g4,g0)
    c: Coincident(g5,g0)
    c: Coincident(g6,g1)
    c: Coincident(g7,g2)
    c: DistanceY(g6) = 74.3
    c: DistanceY(g3,g3) = 71.7
    c: DistanceX(g0,g0) = 11.6
    c: Diameter(g7) = 3
    c: Diameter(g6) = 3
    c: Diameter(g5) = 3
    c: Diameter(g4) = 3
    c: DistanceX(g-3,g4) = 168.2
    c: Coincident(g8,g9)
    c: Coincident(g9,g10)
    c: Coincident(g10,g11)
    c: Coincident(g11,g8)
    c: Horizontal(g8)
    c: Horizontal(g10)
    c: Vertical(g9)
    c: Vertical(g11)
    c: Coincident(g12,g8)
    c: Coincident(g13,g8)
    c: Coincident(g14,g9)
    c: Coincident(g15,g10)
    c: Equal(g3,g11) = 71.7
    c: Equal(g0,g8) = 11.6
    c: Equal(g7,g15) = 3
    c: Equal(g6,g14) = 3
    c: Equal(g5,g13) = 3
    c: Equal(g4,g12) = 3
    c: Horizontal(g6,g15)
    c: Coincident(g16,g17)
    c: Coincident(g17,g18)
    c: Coincident(g18,g19)
    c: Coincident(g19,g16)
    c: Horizontal(g16)
    c: Horizontal(g18)
    c: Vertical(g17)
    c: Vertical(g19)
    c: Coincident(g20,g16)
    c: Coincident(g21,g16)
    c: Coincident(g22,g17)
    c: Coincident(g23,g18)
    c: Equal(g3,g19) = 71.7
    c: Equal(g0,g16) = 11.6
    c: Equal(g7,g23) = 3
    c: Equal(g6,g22) = 3
    c: Equal(g5,g21) = 3
    c: Equal(g4,g20) = 3
    c: Horizontal(g14,g23)
    c: DistanceX(g12,g21) = 168.2
    c: DistanceX(g20,g-4) = 168.2
    c: DistanceX(g5,g13) = 222.4
FEATURE [PartDesign::Pocket] Pocket003  label="Trous fixation entretoise double"
  BaseFeature = -> Pocket002
  Direction = (0,0,-1)
  Length = 5
  Length2 = 5
  Profile = -> Sketch005
  ReferenceAxis = -> Sketch005 [N_Axis]
  Type = 1
FEATURE [Sketcher::SketchObject] Sketch006  label="Sketch trous fixation enjoliveurs"
  ExternalGeometry = -> [Pocket003]
  FullyConstrained = true
  MapMode = 5
  Support = -> [Pocket003]
  sketch-geometry (9):
    g0: Circle CenterX=34.1 CenterY=27.1 CenterZ=0 NormalX=0 NormalY=0 NormalZ=1 AngleXU=0 Radius=1.5
    g1: Circle CenterX=1083.6 CenterY=27.1 CenterZ=0 NormalX=0 NormalY=0 NormalZ=1 AngleXU=0 Radius=1.5
    g2: Circle CenterX=944.6 CenterY=27.1 CenterZ=0 NormalX=0 NormalY=0 NormalZ=1 AngleXU=0 Radius=1.5
    g3: ArcOfCircle CenterX=156.746 CenterY=26.7464 CenterZ=0 NormalX=0 NormalY=0 NormalZ=1 AngleXU=0 Radius=2.5 StartAngle=2.35619 EndAngle=5.49779
    g4: ArcOfCircle CenterX=157.454 CenterY=27.4536 CenterZ=0 NormalX=0 NormalY=0 NormalZ=1 AngleXU=0 Radius=2.5 StartAngle=5.49779 EndAngle=8.63938
    g5: LineSegment StartX=158.514 StartY=24.9787 StartZ=0 EndX=159.221 EndY=25.6858 EndZ=0
    g6: LineSegment StartX=155.686 StartY=29.2213 StartZ=0 EndX=154.979 EndY=28.5142 EndZ=0
    g7: LineSegment StartX=156.746 StartY=26.7464 StartZ=0 EndX=157.454 EndY=27.4536 EndZ=0
    g8: GeomPoint X=157.1 Y=27.1 Z=0
  constraints (22):
    c: Diameter(g0) = 3
    c: DistanceX(g0) = 34.1
    c: DistanceY(g-3,g0) = 30.1
    c: Horizontal(g1,g0)
    c: Diameter(g1) = 3
    c: DistanceX(g1,g-4) = 34.4
    c: Horizontal(g2,g1)
    c: DistanceX(g2,g1) = 139
    c: Diameter(g2) = 3
    c: Tangent(g3,g5) = -1.5708
    c: Tangent(g5,g4) = -1.5708
    c: Tangent(g4,g6) = -1.5708
    c: Tangent(g6,g3) = -1.5708
    c: Equal(g3,g4)
    c: Diameter(g3) = 5
    c: Distance(g6) = 1
    c: Coincident(g7,g3)
    c: Coincident(g7,g4)
    c: Angle(g7,g-1) = 2.35619
    c: Symmetric(g3,g4,g8)
    c: DistanceX(g8) = 157.1
    c: Horizontal(g0,g8)
FEATURE [PartDesign::Pocket] Pocket004  label="Trous fixation enjoliveurs"
  BaseFeature = -> Pocket003
  Direction = (0,0,-1)
  Length = 5
  Length2 = 5
  Profile = -> Sketch006
  ReferenceAxis = -> Sketch006 [N_Axis]
  Type = 1
FEATURE [Sketcher::SketchObject] Sketch007  label="Sketch trous fixation panneau 1"
  ExternalGeometry = -> [Pocket004]
  FullyConstrained = true
  MapMode = 5
  Support = -> [Pocket004]
  sketch-geometry (2):
    g0: Circle CenterX=13 CenterY=20 CenterZ=0 NormalX=0 NormalY=0 NormalZ=1 AngleXU=0 Radius=3
    g1: Circle CenterX=1105 CenterY=20 CenterZ=0 NormalX=0 NormalY=0 NormalZ=1 AngleXU=0 Radius=3
  constraints (6):
    c: Diameter(g0) = 6
    c: DistanceX(g0) = 13
    c: DistanceX(g1,g-3) = 13
    c: Diameter(g1) = 6
    c: Horizontal(g1,g0)
    c: DistanceY(g0) = 20
FEATURE [PartDesign::Pocket] Pocket005  label="Trous fixation panneau 1"
  BaseFeature = -> Pocket004
  Direction = (0,0,-1)
  Length = 5
  Length2 = 5
  Profile = -> Sketch007
  ReferenceAxis = -> Sketch007 [N_Axis]
  Type = 1
FEATURE [Sketcher::SketchObject] Sketch008  label="Sketch trous fixation bloc bois"
  ExternalGeometry = -> [Pocket005]
  FullyConstrained = true
  MapMode = 5
  Support = -> [Pocket005]
  sketch-geometry (4):
    g0: Circle CenterX=13 CenterY=68 CenterZ=0 NormalX=0 NormalY=0 NormalZ=1 AngleXU=0 Radius=1.5
    g1: Circle CenterX=1105 CenterY=68 CenterZ=0 NormalX=0 NormalY=0 NormalZ=1 AngleXU=0 Radius=1.5
    g2: Circle CenterX=90 CenterY=107 CenterZ=0 NormalX=0 NormalY=0 NormalZ=1 AngleXU=0 Radius=1.5
    g3: Circle CenterX=1028 CenterY=107 CenterZ=0 NormalX=0 NormalY=0 NormalZ=1 AngleXU=0 Radius=1.5
  constraints (12):
    c: Diameter(g0) = 3
    c: Diameter(g1) = 3
    c: Diameter(g2) = 3
    c: DistanceX(g2) = 90
    c: DistanceY(g2) = 107
    c: Diameter(g3) = 3
    c: DistanceX(g3,g-5) = 90
    c: Horizontal(g3,g2)
    c: DistanceX(g0) = 13
    c: DistanceX(g1,g-5) = 13
    c: Horizontal(g0,g1)
    c: DistanceY(g0) = 68
FEATURE [PartDesign::Pocket] Pocket006  label="Trous fixation bloc bois"
  BaseFeature = -> Pocket005
  Direction = (0,0,-1)
  Length = 5
  Length2 = 5
  Profile = -> Sketch008
  ReferenceAxis = -> Sketch008 [N_Axis]
  Type = 1
FEATURE [TechDraw::DrawSVGTemplate] Template003 .. Template006  x4 (patterned run collapsed; names and placements below)
  Height = 210
  Orientation = 1
  Width = 297
FEATURE [TechDraw::DrawViewAnnotation] Annotation
  Font = osifont
  LineSpace = 80
  LockPosition = false
  MaxWidth = -1
  Rotation = 0
  ScaleType = 0
  Text = 1 - PCB Vibrato Chorus
  TextSize = 5
  TextStyle = 0
  X = 56.5726
  Y = 172.821
FEATURE [TechDraw::DrawViewAnnotation] Annotation001
  Font = osifont
  LineSpace = 80
  LockPosition = false
  MaxWidth = -1
  Rotation = 0
  ScaleType = 0
  Text = 2 - Entretoise tirettes
  TextSize = 5
  TextStyle = 0
  X = 118.195
  Y = 173.318
FEATURE [TechDraw::DrawViewAnnotation] Annotation002
  Font = osifont
  LineSpace = 80
  LockPosition = false
  MaxWidth = -1
  Rotation = 0
  ScaleType = 0
  Text = 3 - Comm. rotatif vib/chorus
  TextSize = 5
  TextStyle = 0
  X = 241.327
  Y = 172.43
FEATURE [TechDraw::DrawViewAnnotation] Annotation003
  Font = osifont
  LineSpace = 80
  LockPosition = false
  MaxWidth = -1
  Rotation = 0
  ScaleType = 0
  Text = 4 - Maintien enjoliveur boutons vib/ch
  TextSize = 5
  TextStyle = 0
  X = 251.908
  Y = 147.936
FEATURE [TechDraw::DrawViewAnnotation] Annotation004
  Font = osifont
  LineSpace = 80
  LockPosition = false
  MaxWidth = -1
  Rotation = 0
  ScaleType = 0
  Text = 5 - Fixation panneau acier sur supports bois
  TextSize = 5
  TextStyle = 0
  X = 246.384
  Y = 123.299
FEATURE [Sketcher::SketchObject] Sketch009  label="Sketch trous fixation panneau 2"
  ExternalGeometry = -> [Pocket006]
  FullyConstrained = true
  MapMode = 5
  Support = -> [Pocket006]
  sketch-geometry (2):
    g0: Circle CenterX=13 CenterY=96 CenterZ=0 NormalX=0 NormalY=0 NormalZ=1 AngleXU=0 Radius=2
    g1: Circle CenterX=1105 CenterY=96 CenterZ=0 NormalX=0 NormalY=0 NormalZ=1 AngleXU=0 Radius=2
  constraints (6):
    c: Diameter(g0) = 4
    c: DistanceY(g0) = 96
    c: DistanceX(g0) = 13
    c: Diameter(g1) = 4
    c: DistanceY(g1) = 96
    c: DistanceX(g1,g-3) = 13
FEATURE [PartDesign::Hole] Hole001  label="Trous fixation panneau 2"
  BaseFeature = -> Pocket006
  CustomThreadClearance = 0
  Depth = 2281.57
  DepthType = 1
  Diameter = 4
  DrillForDepth = false
  DrillPoint = 1
  DrillPointAngle = 118
  HoleCutCountersinkAngle = 90
  HoleCutCustomValues = false
  HoleCutDepth = 0.5
  HoleCutDiameter = 6.1
  HoleCutType = 2
  ModelThread = false
  Profile = -> Sketch009
  Tapered = false
  TaperedAngle = 90
  ThreadClass = 0
  ThreadDepth = 2281.57
  ThreadDepthType = 0
  ThreadDirection = 0
  ThreadFit = 1
  ThreadSize = 0
  ThreadType = 0
  Threaded = false
  UseCustomThreadClearance = false
FEATURE [PartDesign::Body] Body
  Group = -> [Sketch,Pad,Sketch001,Pocket,LinearPattern,Sketch002,Pocket001,LinearPattern001,Bend,Bend001,Sketch003,Hole,Sketch004,Pocket002,Sketch005,Pocket003,Sketch006,Pocket004,Sketch007,Pocket005,Sketch008,Pocket006,Sketch009,Hole001]
  Origin = -> Origin
  Placement = pos=(100,0,0) rot=(0,0,1;0rad)
  Tip = -> Hole001
FEATURE [TechDraw::DrawViewPart] View003
  CoarseView = false
  Direction = (0,0,1)
  Focus = 100
  HardHidden = false
  IsoCount = 0
  IsoHidden = false
  IsoVisible = false
  LockPosition = false
  Perspective = false
  Rotation = 0
  ScaleType = 2
  SeamHidden = false
  SeamVisible = false
  SmoothHidden = false
  SmoothVisible = false
  Source = -> [Body]
  X = 606.556
  XDirection = (1,0,0)
  Y = 112.424
FEATURE [TechDraw::DrawViewDimension] Dimension026
  AngleOverride = false
  Arbitrary = false
  ArbitraryTolerances = false
  EqualTolerance = true
  ExtensionAngle = 0
  FormatSpec = %.2w
  FormatSpecOverTolerance = %+.2w
  FormatSpecUnderTolerance = %+.2w
  Inverted = false
  LineAngle = 0
  LockPosition = false
  MeasureType = 1
  OverTolerance = 0
  References2D = -> [View003]
  Rotation = 0
  ScaleType = 0
  TheoreticalExact = false
  Type = 1
  UnderTolerance = 0
  X = -512.761
  Y = 47.5133
FEATURE [TechDraw::DrawViewDimension] Dimension028
  AngleOverride = false
  Arbitrary = false
  ArbitraryTolerances = false
  EqualTolerance = true
  ExtensionAngle = 0
  FormatSpec = %.2w
  FormatSpecOverTolerance = %+.2w
  FormatSpecUnderTolerance = %+.2w
  Inverted = false
  LineAngle = 0
  LockPosition = false
  MeasureType = 1
  OverTolerance = 0
  References2D = -> [View003]
  Rotation = 0
  ScaleType = 0
  TheoreticalExact = false
  Type = 1
  UnderTolerance = 0
  X = -189.726
  Y = 37.8731
FEATURE [TechDraw::DrawViewDimension] Dimension030
  AngleOverride = false
  Arbitrary = false
  ArbitraryTolerances = false
  EqualTolerance = true
  ExtensionAngle = 0
  FormatSpec = %.2w
  FormatSpecOverTolerance = %+.2w
  FormatSpecUnderTolerance = %+.2w
  Inverted = false
  LineAngle = 0
  LockPosition = false
  MeasureType = 1
  OverTolerance = 0
  References2D = -> [View003]
  Rotation = 0
  ScaleType = 0
  TheoreticalExact = false
  Type = 1
  UnderTolerance = 0
  X = 117.463
  Y = 29.0478
FEATURE [TechDraw::DrawViewDimension] Dimension031
  AngleOverride = false
  Arbitrary = false
  ArbitraryTolerances = false
  EqualTolerance = true
  ExtensionAngle = 0
  FormatSpec = %.2w
  FormatSpecOverTolerance = %+.2w
  FormatSpecUnderTolerance = %+.2w
  Inverted = false
  LineAngle = 0
  LockPosition = false
  MeasureType = 1
  OverTolerance = 0
  References2D = -> [View003]
  Rotation = 0
  ScaleType = 0
  TheoreticalExact = false
  Type = 1
  UnderTolerance = 0
  X = 95.5584
  Y = 36.9079
FEATURE [TechDraw::DrawViewDimension] Dimension032
  AngleOverride = false
  Arbitrary = false
  ArbitraryTolerances = false
  EqualTolerance = true
  ExtensionAngle = 0
  FormatSpec = %.2w
  FormatSpecOverTolerance = %+.2w
  FormatSpecUnderTolerance = %+.2w
  Inverted = false
  LineAngle = 0
  LockPosition = false
  MeasureType = 1
  OverTolerance = 0
  References2D = -> [View003]
  Rotation = 0
  ScaleType = 0
  TheoreticalExact = false
  Type = 1
  UnderTolerance = 0
  X = 75.055
  Y = 45.6034
FEATURE [TechDraw::DrawViewDimension] Dimension033
  AngleOverride = false
  Arbitrary = false
  ArbitraryTolerances = false
  EqualTolerance = true
  ExtensionAngle = 0
  FormatSpec = %.2w
  FormatSpecOverTolerance = %+.2w
  FormatSpecUnderTolerance = %+.2w
  Inverted = false
  LineAngle = 0
  LockPosition = false
  MeasureType = 1
  OverTolerance = 0
  References2D = -> [View003]
  Rotation = 0
  ScaleType = 0
  TheoreticalExact = false
  Type = 2
  UnderTolerance = 0
  X = -137.701
  Y = 8.10532
FEATURE [TechDraw::DrawViewDimension] Dimension034
  AngleOverride = false
  Arbitrary = false
  ArbitraryTolerances = false
  EqualTolerance = true
  ExtensionAngle = 0
  FormatSpec = %.2w
  FormatSpecOverTolerance = %+.2w
  FormatSpecUnderTolerance = %+.2w
  Inverted = false
  LineAngle = 0
  LockPosition = false
  MeasureType = 1
  OverTolerance = 0
  References2D = -> [View003]
  Rotation = 0
  ScaleType = 0
  TheoreticalExact = false
  Type = 2
  UnderTolerance = 0
  X = -22.6084
  Y = 15.8875
FEATURE [TechDraw::DrawViewDimension] Dimension037
  AngleOverride = false
  Arbitrary = false
  ArbitraryTolerances = false
  EqualTolerance = true
  ExtensionAngle = 0
  FormatSpec = %.2w
  FormatSpecOverTolerance = %+.2w
  FormatSpecUnderTolerance = %+.2w
  Inverted = false
  LineAngle = 0
  LockPosition = false
  MeasureType = 1
  OverTolerance = 0
  References2D = -> [View003]
  Rotation = 0
  ScaleType = 0
  TheoreticalExact = false
  Type = 2
  UnderTolerance = 0
  X = -417.026
  Y = -22.262
FEATURE [TechDraw::DrawViewDimension] Dimension039
  AngleOverride = false
  Arbitrary = false
  ArbitraryTolerances = false
  EqualTolerance = true
  ExtensionAngle = 0
  FormatSpec = %.2w
  FormatSpecOverTolerance = %+.2w
  FormatSpecUnderTolerance = %+.2w
  Inverted = false
  LineAngle = 0
  LockPosition = false
  MeasureType = 1
  OverTolerance = 0
  References2D = -> [View003]
  Rotation = 0
  ScaleType = 0
  TheoreticalExact = false
  Type = 1
  UnderTolerance = 0
  X = 30.8387
  Y = -4.72975
FEATURE [TechDraw::DrawViewDimension] Dimension040
  AngleOverride = false
  Arbitrary = false
  ArbitraryTolerances = false
  EqualTolerance = true
  ExtensionAngle = 0
  FormatSpec = %.2w
  FormatSpecOverTolerance = %+.2w
  FormatSpecUnderTolerance = %+.2w
  Inverted = false
  LineAngle = 0
  LockPosition = false
  MeasureType = 1
  OverTolerance = 0
  References2D = -> [View003]
  Rotation = 0
  ScaleType = 0
  TheoreticalExact = false
  Type = 1
  UnderTolerance = 0
  X = 74.2866
  Y = -4.59319
FEATURE [TechDraw::DrawViewDimension] Dimension041
  AngleOverride = false
  Arbitrary = false
  ArbitraryTolerances = false
  EqualTolerance = true
  ExtensionAngle = 0
  FormatSpec = %.2w
  FormatSpecOverTolerance = %+.2w
  FormatSpecUnderTolerance = %+.2w
  Inverted = false
  LineAngle = 0
  LockPosition = false
  MeasureType = 1
  OverTolerance = 0
  References2D = -> [View003]
  Rotation = 0
  ScaleType = 0
  TheoreticalExact = false
  Type = 1
  UnderTolerance = 0
  X = -41.2139
  Y = -12.5097
FEATURE [TechDraw::DrawViewDimension] Dimension042
  AngleOverride = false
  Arbitrary = false
  ArbitraryTolerances = false
  EqualTolerance = true
  ExtensionAngle = 0
  FormatSpec = %.2w
  FormatSpecOverTolerance = %+.2w
  FormatSpecUnderTolerance = %+.2w
  Inverted = false
  LineAngle = 0
  LockPosition = false
  MeasureType = 1
  OverTolerance = 0
  References2D = -> [View003]
  Rotation = 0
  ScaleType = 0
  TheoreticalExact = false
  Type = 1
  UnderTolerance = 0
  X = -542.94
  Y = -18.1708
FEATURE [TechDraw::DrawViewDimension] Dimension043
  AngleOverride = false
  Arbitrary = false
  ArbitraryTolerances = false
  EqualTolerance = true
  ExtensionAngle = 0
  FormatSpec = %.2w
  FormatSpecOverTolerance = %+.2w
  FormatSpecUnderTolerance = %+.2w
  Inverted = false
  LineAngle = 0
  LockPosition = false
  MeasureType = 1
  OverTolerance = 0
  References2D = -> [View003]
  Rotation = 0
  ScaleType = 0
  TheoreticalExact = false
  Type = 1
  UnderTolerance = 0
  X = -498.135
  Y = -90.4963
FEATURE [TechDraw::DrawViewDimension] Dimension044
  AngleOverride = false
  Arbitrary = false
  ArbitraryTolerances = false
  EqualTolerance = true
  ExtensionAngle = 0
  FormatSpec = %.2w
  FormatSpecOverTolerance = %+.2w
  FormatSpecUnderTolerance = %+.2w
  Inverted = false
  LineAngle = 0
  LockPosition = false
  MeasureType = 1
  OverTolerance = 0
  References2D = -> [View003]
  Rotation = 0
  ScaleType = 0
  TheoreticalExact = false
  Type = 1
  UnderTolerance = 0
  X = -570.325
  Y = 33.069
FEATURE [TechDraw::DrawViewDimension] Dimension049
  AngleOverride = false
  Arbitrary = false
  ArbitraryTolerances = false
  EqualTolerance = true
  ExtensionAngle = 0
  FormatSpec = %.2w
  FormatSpecOverTolerance = %+.2w
  FormatSpecUnderTolerance = %+.2w
  Inverted = false
  LineAngle = 0
  LockPosition = false
  MeasureType = 1
  OverTolerance = 0
  References2D = -> [View003]
  Rotation = 0
  ScaleType = 0
  TheoreticalExact = false
  Type = 1
  UnderTolerance = 0
  X = -471.146
  Y = -15.6643
FEATURE [TechDraw::DrawViewDimension] Dimension056
  AngleOverride = false
  Arbitrary = false
  ArbitraryTolerances = false
  EqualTolerance = true
  ExtensionAngle = 0
  FormatSpec = ⌀%.2w
  FormatSpecOverTolerance = %+.2w
  FormatSpecUnderTolerance = %+.2w
  Inverted = false
  LineAngle = 0
  LockPosition = false
  MeasureType = 1
  OverTolerance = 0
  References2D = -> [View003]
  Rotation = 0
  ScaleType = 0
  TheoreticalExact = false
  Type = 5
  UnderTolerance = 0
  X = -480.705
  Y = 39.1898
FEATURE [TechDraw::DrawViewDimension] Dimension057
  AngleOverride = false
  Arbitrary = false
  ArbitraryTolerances = false
  EqualTolerance = true
  ExtensionAngle = 0
  FormatSpec = ⌀%.2w
  FormatSpecOverTolerance = %+.2w
  FormatSpecUnderTolerance = %+.2w
  Inverted = false
  LineAngle = 0
  LockPosition = false
  MeasureType = 1
  OverTolerance = 0
  References2D = -> [View003]
  Rotation = 0
  ScaleType = 0
  TheoreticalExact = false
  Type = 5
  UnderTolerance = 0
  X = -389.973
  Y = -0.930576
FEATURE [TechDraw::DrawViewDimension] Dimension059
  AngleOverride = false
  Arbitrary = false
  ArbitraryTolerances = false
  EqualTolerance = true
  ExtensionAngle = 0
  FormatSpec = ⌀%.2w
  FormatSpecOverTolerance = %+.2w
  FormatSpecUnderTolerance = %+.2w
  Inverted = false
  LineAngle = 0
  LockPosition = false
  MeasureType = 1
  OverTolerance = 0
  References2D = -> [View003]
  Rotation = 0
  ScaleType = 0
  TheoreticalExact = false
  Type = 5
  UnderTolerance = 0
  X = -448.783
  Y = 5.30557
FEATURE [TechDraw::DrawViewDimension] Dimension060
  AngleOverride = false
  Arbitrary = false
  ArbitraryTolerances = false
  EqualTolerance = true
  ExtensionAngle = 0
  FormatSpec = ⌀%.2w
  FormatSpecOverTolerance = %+.2w
  FormatSpecUnderTolerance = %+.2w
  Inverted = false
  LineAngle = 0
  LockPosition = false
  MeasureType = 1
  OverTolerance = 0
  References2D = -> [View003]
  Rotation = 0
  ScaleType = 0
  TheoreticalExact = false
  Type = 5
  UnderTolerance = 0
  X = -551.205
  Y = -47.6015
FEATURE [TechDraw::DrawViewDimension] Dimension061
  AngleOverride = false
  Arbitrary = false
  ArbitraryTolerances = false
  EqualTolerance = true
  ExtensionAngle = 0
  FormatSpec = ⌀%.2w
  FormatSpecOverTolerance = %+.2w
  FormatSpecUnderTolerance = %+.2w
  Inverted = false
  LineAngle = 0
  LockPosition = false
  MeasureType = 1
  OverTolerance = 0
  References2D = -> [View003]
  Rotation = 0
  ScaleType = 0
  TheoreticalExact = false
  Type = 5
  UnderTolerance = 0
  X = -534.705
  Y = 0.532914
FEATURE [TechDraw::DrawViewDimension] Dimension062
  AngleOverride = false
  Arbitrary = false
  ArbitraryTolerances = false
  EqualTolerance = true
  ExtensionAngle = 0
  FormatSpec = ⌀%.2w
  FormatSpecOverTolerance = %+.2w
  FormatSpecUnderTolerance = %+.2w
  Inverted = false
  LineAngle = 0
  LockPosition = false
  MeasureType = 1
  OverTolerance = 0
  References2D = -> [View003]
  Rotation = 0
  ScaleType = 0
  TheoreticalExact = false
  Type = 5
  UnderTolerance = 0
  X = -517.883
  Y = 34.6494
FEATURE [TechDraw::DrawViewDimension] Dimension063
  AngleOverride = false
  Arbitrary = false
  ArbitraryTolerances = false
  EqualTolerance = true
  ExtensionAngle = 0
  FormatSpec = ⌀%.2w
  FormatSpecOverTolerance = %+.2w
  FormatSpecUnderTolerance = %+.2w
  Inverted = false
  LineAngle = 0
  LockPosition = false
  MeasureType = 1
  OverTolerance = 0
  References2D = -> [View003]
  Rotation = 0
  ScaleType = 0
  TheoreticalExact = false
  Type = 5
  UnderTolerance = 0
  X = -535.523
  Y = -36.384
FEATURE [TechDraw::DrawViewDimension] Dimension064
  AngleOverride = false
  Arbitrary = false
  ArbitraryTolerances = false
  EqualTolerance = true
  ExtensionAngle = 0
  FormatSpec = ⌀%.2w
  FormatSpecOverTolerance = %+.2w
  FormatSpecUnderTolerance = %+.2w
  Inverted = false
  LineAngle = 0
  LockPosition = false
  MeasureType = 1
  OverTolerance = 0
  References2D = -> [View003]
  Rotation = 0
  ScaleType = 0
  TheoreticalExact = false
  Type = 5
  UnderTolerance = 0
  X = -384.93
  Y = -52.478
FEATURE [TechDraw::DrawViewDimension] Dimension065
  AngleOverride = false
  Arbitrary = false
  ArbitraryTolerances = false
  EqualTolerance = true
  ExtensionAngle = 0
  FormatSpec = ⌀%.2w
  FormatSpecOverTolerance = %+.2w
  FormatSpecUnderTolerance = %+.2w
  Inverted = false
  LineAngle = 0
  LockPosition = false
  MeasureType = 1
  OverTolerance = 0
  References2D = -> [View003]
  Rotation = 0
  ScaleType = 0
  TheoreticalExact = false
  Type = 5
  UnderTolerance = 0
  X = -528.418
  Y = 13.847
FEATURE [TechDraw::DrawViewDimension] Dimension066
  AngleOverride = false
  Arbitrary = false
  ArbitraryTolerances = false
  EqualTolerance = true
  ExtensionAngle = 0
  FormatSpec = %.2w
  FormatSpecOverTolerance = %+.2w
  FormatSpecUnderTolerance = %+.2w
  Inverted = false
  LineAngle = 0
  LockPosition = false
  MeasureType = 1
  OverTolerance = 0
  References2D = -> [View003]
  Rotation = 0
  ScaleType = 0
  TheoreticalExact = false
  Type = 2
  UnderTolerance = 0
  X = -582.985
  Y = -29.4191
FEATURE [TechDraw::DrawViewDimension] Dimension067
  AngleOverride = false
  Arbitrary = false
  ArbitraryTolerances = false
  EqualTolerance = true
  ExtensionAngle = 0
  FormatSpec = %.2w
  FormatSpecOverTolerance = %+.2w
  FormatSpecUnderTolerance = %+.2w
  Inverted = false
  LineAngle = 0
  LockPosition = false
  MeasureType = 1
  OverTolerance = 0
  References2D = -> [View003]
  Rotation = 0
  ScaleType = 0
  TheoreticalExact = false
  Type = 2
  UnderTolerance = 0
  X = -477.148
  Y = -67.1086
FEATURE [TechDraw::DrawViewDimension] Dimension068
  AngleOverride = false
  Arbitrary = false
  ArbitraryTolerances = false
  EqualTolerance = true
  ExtensionAngle = 0
  FormatSpec = ⌀%.2w
  FormatSpecOverTolerance = %+.2w
  FormatSpecUnderTolerance = %+.2w
  Inverted = false
  LineAngle = 0
  LockPosition = false
  MeasureType = 1
  OverTolerance = 0
  References2D = -> [View003]
  Rotation = 0
  ScaleType = 0
  TheoreticalExact = false
  Type = 5
  UnderTolerance = 0
  X = -393.969
  Y = 65.9295
FEATURE [TechDraw::DrawViewDimension] Dimension069
  AngleOverride = false
  Arbitrary = false
  ArbitraryTolerances = false
  EqualTolerance = true
  ExtensionAngle = 0
  FormatSpec = %.2w
  FormatSpecOverTolerance = %+.2w
  FormatSpecUnderTolerance = %+.2w
  Inverted = false
  LineAngle = 0
  LockPosition = false
  MeasureType = 1
  OverTolerance = 0
  References2D = -> [View003]
  Rotation = 0
  ScaleType = 0
  TheoreticalExact = false
  Type = 2
  UnderTolerance = 0
  X = -410.731
  Y = 61.1202
FEATURE [TechDraw::DrawViewDimension] Dimension070
  AngleOverride = false
  Arbitrary = false
  ArbitraryTolerances = false
  EqualTolerance = true
  ExtensionAngle = 0
  FormatSpec = %.2w
  FormatSpecOverTolerance = %+.2w
  FormatSpecUnderTolerance = %+.2w
  Inverted = false
  LineAngle = 0
  LockPosition = false
  MeasureType = 1
  OverTolerance = 0
  References2D = -> [View003]
  Rotation = 0
  ScaleType = 0
  TheoreticalExact = false
  Type = 2
  UnderTolerance = 0
  X = -367.221
  Y = 40.8398
FEATURE [TechDraw::DrawViewDimension] Dimension071
  AngleOverride = false
  Arbitrary = false
  ArbitraryTolerances = false
  EqualTolerance = true
  ExtensionAngle = 0
  FormatSpec = %.2w
  FormatSpecOverTolerance = %+.2w
  FormatSpecUnderTolerance = %+.2w
  Inverted = false
  LineAngle = 0
  LockPosition = false
  MeasureType = 1
  OverTolerance = 0
  References2D = -> [View003]
  Rotation = 0
  ScaleType = 0
  TheoreticalExact = false
  Type = 1
  UnderTolerance = 0
  X = -469.65
  Y = 92.0198
FEATURE [TechDraw::DrawViewDimension] Dimension072
  AngleOverride = false
  Arbitrary = false
  ArbitraryTolerances = false
  EqualTolerance = true
  ExtensionAngle = 0
  FormatSpec = %.2w
  FormatSpecOverTolerance = %+.2w
  FormatSpecUnderTolerance = %+.2w
  Inverted = false
  LineAngle = 0
  LockPosition = false
  MeasureType = 1
  OverTolerance = 0
  References2D = -> [View003]
  Rotation = 0
  ScaleType = 0
  TheoreticalExact = false
  Type = 2
  UnderTolerance = 0
  X = -451.074
  Y = 56.3201
FEATURE [TechDraw::DrawViewDimension] Dimension073
  AngleOverride = false
  Arbitrary = false
  ArbitraryTolerances = false
  EqualTolerance = true
  ExtensionAngle = 0
  FormatSpec = %.2w
  FormatSpecOverTolerance = %+.2w
  FormatSpecUnderTolerance = %+.2w
  Inverted = false
  LineAngle = 0
  LockPosition = false
  MeasureType = 1
  OverTolerance = 0
  References2D = -> [View003]
  Rotation = 0
  ScaleType = 0
  TheoreticalExact = false
  Type = 2
  UnderTolerance = 0
  X = -357.152
  Y = -63.5665
FEATURE [TechDraw::DrawViewDimension] Dimension074
  AngleOverride = false
  Arbitrary = false
  ArbitraryTolerances = false
  EqualTolerance = true
  ExtensionAngle = 0
  FormatSpec = %.2w
  FormatSpecOverTolerance = %+.2w
  FormatSpecUnderTolerance = %+.2w
  Inverted = false
  LineAngle = 0
  LockPosition = false
  MeasureType = 1
  OverTolerance = 0
  References2D = -> [View003]
  Rotation = 0
  ScaleType = 0
  TheoreticalExact = false
  Type = 1
  UnderTolerance = 0
  X = -481.996
  Y = -100.391
FEATURE [TechDraw::DrawViewDimension] Dimension075
  AngleOverride = false
  Arbitrary = false
  ArbitraryTolerances = false
  EqualTolerance = true
  ExtensionAngle = 0
  FormatSpec = %.2w
  FormatSpecOverTolerance = %+.2w
  FormatSpecUnderTolerance = %+.2w
  Inverted = false
  LineAngle = 0
  LockPosition = false
  MeasureType = 1
  OverTolerance = 0
  References2D = -> [View003]
  Rotation = 0
  ScaleType = 0
  TheoreticalExact = false
  Type = 1
  UnderTolerance = 0
  X = -535.184
  Y = -81.9578
FEATURE [TechDraw::DrawViewDimension] Dimension076
  AngleOverride = false
  Arbitrary = false
  ArbitraryTolerances = false
  EqualTolerance = true
  ExtensionAngle = 0
  FormatSpec = %.2w
  FormatSpecOverTolerance = %+.2w
  FormatSpecUnderTolerance = %+.2w
  Inverted = false
  LineAngle = 0
  LockPosition = false
  MeasureType = 1
  OverTolerance = 0
  References2D = -> [View003]
  Rotation = 0
  ScaleType = 0
  TheoreticalExact = false
  Type = 1
  UnderTolerance = 0
  X = -552.65
  Y = -38.5224
FEATURE [TechDraw::DrawViewDimension] Dimension077
  AngleOverride = false
  Arbitrary = false
  ArbitraryTolerances = false
  EqualTolerance = true
  ExtensionAngle = 0
  FormatSpec = %.2w
  FormatSpecOverTolerance = %+.2w
  FormatSpecUnderTolerance = %+.2w
  Inverted = false
  LineAngle = 0
  LockPosition = false
  MeasureType = 1
  OverTolerance = 0
  References2D = -> [View003]
  Rotation = 0
  ScaleType = 0
  TheoreticalExact = false
  Type = 2
  UnderTolerance = 0
  X = -554.744
  Y = -66.5
FEATURE [TechDraw::DrawViewDimension] Dimension078
  AngleOverride = false
  Arbitrary = false
  ArbitraryTolerances = false
  EqualTolerance = true
  ExtensionAngle = 0
  FormatSpec = %.2w
  FormatSpecOverTolerance = %+.2w
  FormatSpecUnderTolerance = %+.2w
  Inverted = false
  LineAngle = 0
  LockPosition = false
  MeasureType = 1
  OverTolerance = 0
  References2D = -> [View003]
  Rotation = 0
  ScaleType = 0
  TheoreticalExact = false
  Type = 2
  UnderTolerance = 0
  X = -571.916
  Y = -41.4397
FEATURE [TechDraw::DrawViewDimension] Dimension079
  AngleOverride = false
  Arbitrary = false
  ArbitraryTolerances = false
  EqualTolerance = true
  ExtensionAngle = 0
  FormatSpec = %.2w
  FormatSpecOverTolerance = %+.2w
  FormatSpecUnderTolerance = %+.2w
  Inverted = false
  LineAngle = 0
  LockPosition = false
  MeasureType = 1
  OverTolerance = 0
  References2D = -> [View003]
  Rotation = 0
  ScaleType = 0
  TheoreticalExact = false
  Type = 2
  UnderTolerance = 0
  X = -532.526
  Y = -63.0484
FEATURE [TechDraw::DrawViewDimension] Dimension080
  AngleOverride = false
  Arbitrary = false
  ArbitraryTolerances = false
  EqualTolerance = true
  ExtensionAngle = 0
  FormatSpec = ⌀%.2w
  FormatSpecOverTolerance = %+.2w
  FormatSpecUnderTolerance = %+.2w
  Inverted = false
  LineAngle = 0
  LockPosition = false
  MeasureType = 1
  OverTolerance = 0
  References2D = -> [View003]
  Rotation = 0
  ScaleType = 0
  TheoreticalExact = false
  Type = 5
  UnderTolerance = 0
  X = -497.666
  Y = 11.5993
FEATURE [TechDraw::DrawViewPart] View004
  CoarseView = false
  Direction = (0,0,1)
  Focus = 100
  HardHidden = false
  IsoCount = 0
  IsoHidden = false
  IsoVisible = false
  LockPosition = false
  Perspective = false
  Rotation = 0
  ScaleType = 0
  SeamHidden = false
  SeamVisible = false
  SmoothHidden = false
  SmoothVisible = false
  Source = -> [Body]
  X = -311.844
  XDirection = (1,0,0)
  Y = 108.916
FEATURE [TechDraw::DrawViewDimension] Dimension081
  AngleOverride = false
  Arbitrary = false
  ArbitraryTolerances = false
  EqualTolerance = true
  ExtensionAngle = 0
  FormatSpec = %.2w
  FormatSpecOverTolerance = %+.2w
  FormatSpecUnderTolerance = %+.2w
  Inverted = false
  LineAngle = 0
  LockPosition = false
  MeasureType = 1
  OverTolerance = 0
  References2D = -> [View004]
  Rotation = 0
  ScaleType = 0
  TheoreticalExact = false
  Type = 1
  UnderTolerance = 0
  X = 538.072
  Y = -82.5239
FEATURE [TechDraw::DrawViewDimension] Dimension082
  AngleOverride = false
  Arbitrary = false
  ArbitraryTolerances = false
  EqualTolerance = true
  ExtensionAngle = 0
  FormatSpec = %.2w
  FormatSpecOverTolerance = %+.2w
  FormatSpecUnderTolerance = %+.2w
  Inverted = false
  LineAngle = 0
  LockPosition = false
  MeasureType = 1
  OverTolerance = 0
  References2D = -> [View004]
  Rotation = 0
  ScaleType = 0
  TheoreticalExact = false
  Type = 1
  UnderTolerance = 0
  X = 473.825
  Y = -92.6188
FEATURE [TechDraw::DrawViewDimension] Dimension083
  AngleOverride = false
  Arbitrary = false
  ArbitraryTolerances = false
  EqualTolerance = true
  ExtensionAngle = 0
  FormatSpec = %.2w
  FormatSpecOverTolerance = %+.2w
  FormatSpecUnderTolerance = %+.2w
  Inverted = false
  LineAngle = 0
  LockPosition = false
  MeasureType = 1
  OverTolerance = 0
  References2D = -> [View004]
  Rotation = 0
  ScaleType = 0
  TheoreticalExact = false
  Type = 2
  UnderTolerance = 0
  X = 453.547
  Y = -67.7174
FEATURE [TechDraw::DrawViewDimension] Dimension084
  AngleOverride = false
  Arbitrary = false
  ArbitraryTolerances = false
  EqualTolerance = true
  ExtensionAngle = 0
  FormatSpec = %.2w
  FormatSpecOverTolerance = %+.2w
  FormatSpecUnderTolerance = %+.2w
  Inverted = false
  LineAngle = 0
  LockPosition = false
  MeasureType = 1
  OverTolerance = 0
  References2D = -> [View004]
  Rotation = 0
  ScaleType = 0
  TheoreticalExact = false
  Type = 2
  UnderTolerance = 0
  X = 574.223
  Y = -37.6232
FEATURE [TechDraw::DrawViewDimension] Dimension085
  AngleOverride = false
  Arbitrary = false
  ArbitraryTolerances = false
  EqualTolerance = true
  ExtensionAngle = 0
  FormatSpec = %.2w
  FormatSpecOverTolerance = %+.2w
  FormatSpecUnderTolerance = %+.2w
  Inverted = false
  LineAngle = 0
  LockPosition = false
  MeasureType = 1
  OverTolerance = 0
  References2D = -> [View004]
  Rotation = 0
  ScaleType = 0
  TheoreticalExact = false
  Type = 1
  UnderTolerance = 0
  X = 551.813
  Y = -43.4322
FEATURE [TechDraw::DrawViewDimension] Dimension086
  AngleOverride = false
  Arbitrary = false
  ArbitraryTolerances = false
  EqualTolerance = true
  ExtensionAngle = 0
  FormatSpec = %.2w
  FormatSpecOverTolerance = %+.2w
  FormatSpecUnderTolerance = %+.2w
  Inverted = false
  LineAngle = 0
  LockPosition = false
  MeasureType = 1
  OverTolerance = 0
  References2D = -> [View004]
  Rotation = 0
  ScaleType = 0
  TheoreticalExact = false
  Type = 1
  UnderTolerance = 0
  X = 552.169
  Y = 1.10752
FEATURE [TechDraw::DrawViewDimension] Dimension087
  AngleOverride = false
  Arbitrary = false
  ArbitraryTolerances = false
  EqualTolerance = true
  ExtensionAngle = 0
  FormatSpec = %.2w
  FormatSpecOverTolerance = %+.2w
  FormatSpecUnderTolerance = %+.2w
  Inverted = false
  LineAngle = 0
  LockPosition = false
  MeasureType = 1
  OverTolerance = 0
  References2D = -> [View004]
  Rotation = 0
  ScaleType = 0
  TheoreticalExact = false
  Type = 1
  UnderTolerance = 0
  X = 552.233
  Y = 38.5869
FEATURE [TechDraw::DrawViewDimension] Dimension088
  AngleOverride = false
  Arbitrary = false
  ArbitraryTolerances = false
  EqualTolerance = true
  ExtensionAngle = 0
  FormatSpec = %.2w
  FormatSpecOverTolerance = %+.2w
  FormatSpecUnderTolerance = %+.2w
  Inverted = false
  LineAngle = 0
  LockPosition = false
  MeasureType = 1
  OverTolerance = 0
  References2D = -> [View004]
  Rotation = 0
  ScaleType = 0
  TheoreticalExact = false
  Type = 2
  UnderTolerance = 0
  X = 585.79
  Y = -30.257
FEATURE [TechDraw::DrawViewDimension] Dimension089
  AngleOverride = false
  Arbitrary = false
  ArbitraryTolerances = false
  EqualTolerance = true
  ExtensionAngle = 0
  FormatSpec = %.2w
  FormatSpecOverTolerance = %+.2w
  FormatSpecUnderTolerance = %+.2w
  Inverted = false
  LineAngle = 0
  LockPosition = false
  MeasureType = 1
  OverTolerance = 0
  References2D = -> [View004]
  Rotation = 0
  ScaleType = 0
  TheoreticalExact = false
  Type = 2
  UnderTolerance = 0
  X = 538.046
  Y = -67.6018
FEATURE [TechDraw::DrawViewDimension] Dimension090
  AngleOverride = false
  Arbitrary = false
  ArbitraryTolerances = false
  EqualTolerance = true
  ExtensionAngle = 0
  FormatSpec = %.2w
  FormatSpecOverTolerance = %+.2w
  FormatSpecUnderTolerance = %+.2w
  Inverted = false
  LineAngle = 0
  LockPosition = false
  MeasureType = 1
  OverTolerance = 0
  References2D = -> [View004]
  Rotation = 0
  ScaleType = 0
  TheoreticalExact = false
  Type = 1
  UnderTolerance = 0
  X = 470.405
  Y = 66.2656
FEATURE [TechDraw::DrawViewDimension] Dimension091
  AngleOverride = false
  Arbitrary = false
  ArbitraryTolerances = false
  EqualTolerance = true
  ExtensionAngle = 0
  FormatSpec = %.2w
  FormatSpecOverTolerance = %+.2w
  FormatSpecUnderTolerance = %+.2w
  Inverted = false
  LineAngle = 0
  LockPosition = false
  MeasureType = 1
  OverTolerance = 0
  References2D = -> [View004]
  Rotation = 0
  ScaleType = 0
  TheoreticalExact = false
  Type = 2
  UnderTolerance = 0
  X = 366.644
  Y = 59.135
FEATURE [TechDraw::DrawViewDimension] Dimension092
  AngleOverride = false
  Arbitrary = false
  ArbitraryTolerances = false
  EqualTolerance = true
  ExtensionAngle = 0
  FormatSpec = %.2w
  FormatSpecOverTolerance = %+.2w
  FormatSpecUnderTolerance = %+.2w
  Inverted = false
  LineAngle = 0
  LockPosition = false
  MeasureType = 1
  OverTolerance = 0
  References2D = -> [View004]
  Rotation = 0
  ScaleType = 0
  TheoreticalExact = false
  Type = 2
  UnderTolerance = 0
  X = 345.035
  Y = 37.1524
FEATURE [TechDraw::DrawViewDimension] Dimension093
  AngleOverride = false
  Arbitrary = false
  ArbitraryTolerances = false
  EqualTolerance = true
  ExtensionAngle = 0
  FormatSpec = ⌀%.2w
  FormatSpecOverTolerance = %+.2w
  FormatSpecUnderTolerance = %+.2w
  Inverted = false
  LineAngle = 0
  LockPosition = false
  MeasureType = 1
  OverTolerance = 0
  References2D = -> [View004]
  Rotation = 0
  ScaleType = 0
  TheoreticalExact = false
  Type = 5
  UnderTolerance = 0
  X = 391.314
  Y = 68.2698
FEATURE [TechDraw::DrawViewDimension] Dimension094
  AngleOverride = false
  Arbitrary = false
  ArbitraryTolerances = false
  EqualTolerance = true
  ExtensionAngle = 0
  FormatSpec = ⌀%.2w
  FormatSpecOverTolerance = %+.2w
  FormatSpecUnderTolerance = %+.2w
  Inverted = false
  LineAngle = 0
  LockPosition = false
  MeasureType = 1
  OverTolerance = 0
  References2D = -> [View004]
  Rotation = 0
  ScaleType = 0
  TheoreticalExact = false
  Type = 5
  UnderTolerance = 0
  X = 388.328
  Y = -1.31593
FEATURE [TechDraw::DrawViewDimension] Dimension095
  AngleOverride = false
  Arbitrary = false
  ArbitraryTolerances = false
  EqualTolerance = true
  ExtensionAngle = 0
  FormatSpec = ⌀%.2w
  FormatSpecOverTolerance = %+.2w
  FormatSpecUnderTolerance = %+.2w
  Inverted = false
  LineAngle = 0
  LockPosition = false
  MeasureType = 1
  OverTolerance = 0
  References2D = -> [View004]
  Rotation = 0
  ScaleType = 0
  TheoreticalExact = false
  Type = 5
  UnderTolerance = 0
  X = 506.307
  Y = 20.2396
FEATURE [TechDraw::DrawViewDimension] Dimension096
  AngleOverride = false
  Arbitrary = false
  ArbitraryTolerances = false
  EqualTolerance = true
  ExtensionAngle = 0
  FormatSpec = ⌀%.2w
  FormatSpecOverTolerance = %+.2w
  FormatSpecUnderTolerance = %+.2w
  Inverted = false
  LineAngle = 0
  LockPosition = false
  MeasureType = 1
  OverTolerance = 0
  References2D = -> [View004]
  Rotation = 0
  ScaleType = 0
  TheoreticalExact = false
  Type = 5
  UnderTolerance = 0
  X = 499.196
  Y = -3.83691
FEATURE [TechDraw::DrawViewDimension] Dimension097
  AngleOverride = false
  Arbitrary = false
  ArbitraryTolerances = false
  EqualTolerance = true
  ExtensionAngle = 0
  FormatSpec = %.2w
  FormatSpecOverTolerance = %+.2w
  FormatSpecUnderTolerance = %+.2w
  Inverted = false
  LineAngle = 0
  LockPosition = false
  MeasureType = 1
  OverTolerance = 0
  References2D = -> [View004]
  Rotation = 0
  ScaleType = 0
  TheoreticalExact = false
  Type = 2
  UnderTolerance = 0
  X = 565.847
  Y = -44.3585
FEATURE [TechDraw::DrawViewDimension] Dimension098
  AngleOverride = false
  Arbitrary = false
  ArbitraryTolerances = false
  EqualTolerance = true
  ExtensionAngle = 0
  FormatSpec = %.2w
  FormatSpecOverTolerance = %+.2w
  FormatSpecUnderTolerance = %+.2w
  Inverted = false
  LineAngle = 0
  LockPosition = false
  MeasureType = 1
  OverTolerance = 0
  References2D = -> [View004]
  Rotation = 0
  ScaleType = 0
  TheoreticalExact = false
  Type = 2
  UnderTolerance = 0
  X = 528.819
  Y = -62.9641
FEATURE [TechDraw::DrawViewDimension] Dimension099
  AngleOverride = false
  Arbitrary = false
  ArbitraryTolerances = false
  EqualTolerance = true
  ExtensionAngle = 0
  FormatSpec = %.2w
  FormatSpecOverTolerance = %+.2w
  FormatSpecUnderTolerance = %+.2w
  Inverted = false
  LineAngle = 0
  LockPosition = false
  MeasureType = 1
  OverTolerance = 0
  References2D = -> [View004]
  Rotation = 0
  ScaleType = 0
  TheoreticalExact = false
  Type = 1
  UnderTolerance = 0
  X = 539.744
  Y = -30.104
FEATURE [TechDraw::DrawViewDimension] Dimension100
  AngleOverride = false
  Arbitrary = false
  ArbitraryTolerances = false
  EqualTolerance = true
  ExtensionAngle = 0
  FormatSpec = %.2w
  FormatSpecOverTolerance = %+.2w
  FormatSpecUnderTolerance = %+.2w
  Inverted = false
  LineAngle = 0
  LockPosition = false
  MeasureType = 1
  OverTolerance = 0
  References2D = -> [View004]
  Rotation = 0
  ScaleType = 0
  TheoreticalExact = false
  Type = 2
  UnderTolerance = 0
  X = 365.185
  Y = -63.6233
FEATURE [TechDraw::DrawViewDimension] Dimension101
  AngleOverride = false
  Arbitrary = false
  ArbitraryTolerances = false
  EqualTolerance = true
  ExtensionAngle = 0
  FormatSpec = %.2w
  FormatSpecOverTolerance = %+.2w
  FormatSpecUnderTolerance = %+.2w
  Inverted = false
  LineAngle = 0
  LockPosition = false
  MeasureType = 1
  OverTolerance = 0
  References2D = -> [View004]
  Rotation = 0
  ScaleType = 0
  TheoreticalExact = false
  Type = 1
  UnderTolerance = 0
  X = 471.737
  Y = -17.586
FEATURE [TechDraw::DrawViewDimension] Dimension102
  AngleOverride = false
  Arbitrary = false
  ArbitraryTolerances = false
  EqualTolerance = true
  ExtensionAngle = 0
  FormatSpec = ⌀%.2w
  FormatSpecOverTolerance = %+.2w
  FormatSpecUnderTolerance = %+.2w
  Inverted = false
  LineAngle = 0
  LockPosition = false
  MeasureType = 1
  OverTolerance = 0
  References2D = -> [View004]
  Rotation = 0
  ScaleType = 0
  TheoreticalExact = false
  Type = 5
  UnderTolerance = 0
  X = 376.65
  Y = -35.2585
FEATURE [TechDraw::DrawViewDimension] Dimension103
  AngleOverride = false
  Arbitrary = false
  ArbitraryTolerances = false
  EqualTolerance = true
  ExtensionAngle = 0
  FormatSpec = ⌀%.2w
  FormatSpecOverTolerance = %+.2w
  FormatSpecUnderTolerance = %+.2w
  Inverted = false
  LineAngle = 0
  LockPosition = false
  MeasureType = 1
  OverTolerance = 0
  References2D = -> [View004]
  Rotation = 0
  ScaleType = 0
  TheoreticalExact = false
  Type = 5
  UnderTolerance = 0
  X = 531.967
  Y = -39.8277
FEATURE [TechDraw::DrawViewDimension] Dimension104
  AngleOverride = false
  Arbitrary = false
  ArbitraryTolerances = false
  EqualTolerance = true
  ExtensionAngle = 0
  FormatSpec = ⌀%.2w
  FormatSpecOverTolerance = %+.2w
  FormatSpecUnderTolerance = %+.2w
  Inverted = false
  LineAngle = 0
  LockPosition = false
  MeasureType = 1
  OverTolerance = 0
  References2D = -> [View004]
  Rotation = 0
  ScaleType = 0
  TheoreticalExact = false
  Type = 5
  UnderTolerance = 0
  X = 541.21
  Y = -48.275
FEATURE [TechDraw::DrawViewDimension] Dimension105
  AngleOverride = false
  Arbitrary = false
  ArbitraryTolerances = false
  EqualTolerance = true
  ExtensionAngle = 0
  FormatSpec = ⌀%.2w
  FormatSpecOverTolerance = %+.2w
  FormatSpecUnderTolerance = %+.2w
  Inverted = false
  LineAngle = 0
  LockPosition = false
  MeasureType = 1
  OverTolerance = 0
  References2D = -> [View004]
  Rotation = 0
  ScaleType = 0
  TheoreticalExact = false
  Type = 5
  UnderTolerance = 0
  X = 537.748
  Y = 1.01408
FEATURE [TechDraw::DrawViewDimension] Dimension106
  AngleOverride = false
  Arbitrary = false
  ArbitraryTolerances = false
  EqualTolerance = true
  ExtensionAngle = 0
  FormatSpec = %.2w
  FormatSpecOverTolerance = %+.2w
  FormatSpecUnderTolerance = %+.2w
  Inverted = false
  LineAngle = 0
  LockPosition = false
  MeasureType = 1
  OverTolerance = 0
  References2D = -> [View004]
  Rotation = 0
  ScaleType = 0
  TheoreticalExact = false
  Type = 2
  UnderTolerance = 0
  X = 451.521
  Y = 57.1144
FEATURE [TechDraw::DrawViewDimension] Dimension107
  AngleOverride = false
  Arbitrary = false
  ArbitraryTolerances = false
  EqualTolerance = true
  ExtensionAngle = 0
  FormatSpec = %.2w
  FormatSpecOverTolerance = %+.2w
  FormatSpecUnderTolerance = %+.2w
  Inverted = false
  LineAngle = 0
  LockPosition = false
  MeasureType = 1
  OverTolerance = 0
  References2D = -> [View004]
  Rotation = 0
  ScaleType = 0
  TheoreticalExact = false
  Type = 1
  UnderTolerance = 0
  X = 511.558
  Y = 53.064
FEATURE [TechDraw::DrawViewDimension] Dimension108
  AngleOverride = false
  Arbitrary = false
  ArbitraryTolerances = false
  EqualTolerance = true
  ExtensionAngle = 0
  FormatSpec = ⌀%.2w
  FormatSpecOverTolerance = %+.2w
  FormatSpecUnderTolerance = %+.2w
  Inverted = false
  LineAngle = 0
  LockPosition = false
  MeasureType = 1
  OverTolerance = 0
  References2D = -> [View004]
  Rotation = 0
  ScaleType = 0
  TheoreticalExact = false
  Type = 5
  UnderTolerance = 0
  X = 480.672
  Y = 41.7713
FEATURE [TechDraw::DrawPage] Page004  label="vue-droite-positions-et-diamètres"
  KeepUpdated = true
  NextBalloonIndex = 1
  ProjectionType = 0
  Template = -> Template004
  Views = -> [View004,Dimension081,Dimension082,Dimension083,Dimension084,Dimension085,Dimension086,Dimension087,Dimension088,Dimension089,Dimension090,Dimension091,Dimension092,Dimension093,Dimension094,Dimension095,Dimension096,Dimension097,Dimension098,Dimension099,Dimension100,Dimension101,Dimension102,Dimension103,Dimension104,Dimension105,Dimension106,Dimension107,Dimension108]
FEATURE [TechDraw::DrawViewPart] View005
  CoarseView = false
  Direction = (0,0,1)
  Focus = 100
  HardHidden = false
  IsoCount = 0
  IsoHidden = false
  IsoVisible = false
  LockPosition = false
  Perspective = false
  Rotation = 0
  Scale = 0.25
  ScaleType = 2
  SeamHidden = false
  SeamVisible = false
  SmoothHidden = false
  SmoothVisible = false
  Source = -> [Body]
  X = 149.749
  XDirection = (1,0,0)
  Y = 110.586
FEATURE [TechDraw::DrawViewDimension] Dimension109
  AngleOverride = false
  Arbitrary = false
  ArbitraryTolerances = false
  EqualTolerance = true
  ExtensionAngle = 0
  FormatSpec = %.2w
  FormatSpecOverTolerance = %+.2w
  FormatSpecUnderTolerance = %+.2w
  Inverted = false
  LineAngle = 0
  LockPosition = false
  MeasureType = 1
  OverTolerance = 0
  References2D = -> [View005]
  Rotation = 0
  Scale = 0.25
  ScaleType = 0
  TheoreticalExact = false
  Type = 1
  UnderTolerance = 0
  X = -116.842
  Y = 30.9544
FEATURE [TechDraw::DrawViewDimension] Dimension110
  AngleOverride = false
  Arbitrary = false
  ArbitraryTolerances = false
  EqualTolerance = true
  ExtensionAngle = 0
  FormatSpec = %.2w
  FormatSpecOverTolerance = %+.2w
  FormatSpecUnderTolerance = %+.2w
  Inverted = false
  LineAngle = 0
  LockPosition = false
  MeasureType = 1
  OverTolerance = 0
  References2D = -> [View005]
  Rotation = 0
  Scale = 0.25
  ScaleType = 0
  TheoreticalExact = false
  Type = 1
  UnderTolerance = 0
  X = -75.8059
  Y = 38.753
FEATURE [TechDraw::DrawViewDimension] Dimension111
  AngleOverride = false
  Arbitrary = false
  ArbitraryTolerances = false
  EqualTolerance = true
  ExtensionAngle = 0
  FormatSpec = %.2w
  FormatSpecOverTolerance = %+.2w
  FormatSpecUnderTolerance = %+.2w
  Inverted = false
  LineAngle = 0
  LockPosition = false
  MeasureType = 1
  OverTolerance = 0
  References2D = -> [View005]
  Rotation = 0
  Scale = 0.25
  ScaleType = 0
  TheoreticalExact = false
  Type = 1
  UnderTolerance = 0
  X = -61.0878
  Y = 13.2922
FEATURE [TechDraw::DrawViewDimension] Dimension112
  AngleOverride = false
  Arbitrary = false
  ArbitraryTolerances = false
  EqualTolerance = true
  ExtensionAngle = 0
  FormatSpec = %.2w
  FormatSpecOverTolerance = %+.2w
  FormatSpecUnderTolerance = %+.2w
  Inverted = false
  LineAngle = 0
  LockPosition = false
  MeasureType = 1
  OverTolerance = 0
  References2D = -> [View005]
  Rotation = 0
  Scale = 0.25
  ScaleType = 0
  TheoreticalExact = false
  Type = 2
  UnderTolerance = 0
  X = -88.0569
  Y = -8.56338
FEATURE [TechDraw::DrawViewDimension] Dimension113
  AngleOverride = false
  Arbitrary = false
  ArbitraryTolerances = false
  EqualTolerance = true
  ExtensionAngle = 0
  FormatSpec = %.2w
  FormatSpecOverTolerance = %+.2w
  FormatSpecUnderTolerance = %+.2w
  Inverted = false
  LineAngle = 0
  LockPosition = false
  MeasureType = 1
  OverTolerance = 0
  References2D = -> [View005]
  Rotation = 0
  Scale = 0.25
  ScaleType = 0
  TheoreticalExact = false
  Type = 1
  UnderTolerance = 0
  X = -23.5075
  Y = 30.9197
FEATURE [TechDraw::DrawViewDimension] Dimension114
  AngleOverride = false
  Arbitrary = false
  ArbitraryTolerances = false
  EqualTolerance = true
  ExtensionAngle = 0
  FormatSpec = %.2w
  FormatSpecOverTolerance = %+.2w
  FormatSpecUnderTolerance = %+.2w
  Inverted = false
  LineAngle = 0
  LockPosition = false
  MeasureType = 1
  OverTolerance = 0
  References2D = -> [View005]
  Rotation = 0
  Scale = 0.25
  ScaleType = 0
  TheoreticalExact = false
  Type = 1
  UnderTolerance = 0
  X = -4.13445
  Y = 13.2964
FEATURE [TechDraw::DrawViewDimension] Dimension115
  AngleOverride = false
  Arbitrary = false
  ArbitraryTolerances = false
  EqualTolerance = true
  ExtensionAngle = 0
  FormatSpec = %.2w
  FormatSpecOverTolerance = %+.2w
  FormatSpecUnderTolerance = %+.2w
  Inverted = false
  LineAngle = 0
  LockPosition = false
  MeasureType = 1
  OverTolerance = 0
  References2D = -> [View005]
  Rotation = 0
  Scale = 0.25
  ScaleType = 0
  TheoreticalExact = false
  Type = 1
  UnderTolerance = 0
  X = 30.0936
  Y = 30.9197
FEATURE [TechDraw::DrawViewDimension] Dimension116
  AngleOverride = false
  Arbitrary = false
  ArbitraryTolerances = false
  EqualTolerance = true
  ExtensionAngle = 0
  FormatSpec = %.2w
  FormatSpecOverTolerance = %+.2w
  FormatSpecUnderTolerance = %+.2w
  Inverted = false
  LineAngle = 0
  LockPosition = false
  MeasureType = 1
  OverTolerance = 0
  References2D = -> [View005]
  Rotation = 0
  Scale = 0.25
  ScaleType = 0
  TheoreticalExact = false
  Type = 1
  UnderTolerance = 0
  X = 74.9722
  Y = 31.0265
FEATURE [TechDraw::DrawViewDimension] Dimension117
  AngleOverride = false
  Arbitrary = false
  ArbitraryTolerances = false
  EqualTolerance = true
  ExtensionAngle = 0
  FormatSpec = %.2w
  FormatSpecOverTolerance = %+.2w
  FormatSpecUnderTolerance = %+.2w
  Inverted = false
  LineAngle = 0
  LockPosition = false
  MeasureType = 1
  OverTolerance = 0
  References2D = -> [View005]
  Rotation = 0
  Scale = 0.25
  ScaleType = 0
  TheoreticalExact = false
  Type = 1
  UnderTolerance = 0
  X = 39.9286
  Y = 13.407
FEATURE [TechDraw::DrawViewDimension] Dimension118
  AngleOverride = false
  Arbitrary = false
  ArbitraryTolerances = false
  EqualTolerance = true
  ExtensionAngle = 0
  FormatSpec = %.2w
  FormatSpecOverTolerance = %+.2w
  FormatSpecUnderTolerance = %+.2w
  Inverted = false
  LineAngle = 0
  LockPosition = false
  MeasureType = 1
  OverTolerance = 0
  References2D = -> [View005]
  Rotation = 0
  Scale = 0.25
  ScaleType = 0
  TheoreticalExact = false
  Type = 2
  UnderTolerance = 0
  X = 83.5201
  Y = -9.19594
FEATURE [TechDraw::DrawViewDimension] Dimension119
  AngleOverride = false
  Arbitrary = false
  ArbitraryTolerances = false
  EqualTolerance = true
  ExtensionAngle = 0
  FormatSpec = %.2w
  FormatSpecOverTolerance = %+.2w
  FormatSpecUnderTolerance = %+.2w
  Inverted = false
  LineAngle = 0
  LockPosition = false
  MeasureType = 1
  OverTolerance = 0
  References2D = -> [View005]
  Rotation = 0
  Scale = 0.25
  ScaleType = 0
  TheoreticalExact = false
  Type = 1
  UnderTolerance = 0
  X = 117.552
  Y = 31.0437
FEATURE [TechDraw::DrawViewDimension] Dimension120
  AngleOverride = false
  Arbitrary = false
  ArbitraryTolerances = false
  EqualTolerance = true
  ExtensionAngle = 0
  FormatSpec = %.2w
  FormatSpecOverTolerance = %+.2w
  FormatSpecUnderTolerance = %+.2w
  Inverted = false
  LineAngle = 0
  LockPosition = false
  MeasureType = 1
  OverTolerance = 0
  References2D = -> [View005]
  Rotation = 0
  Scale = 0.25
  ScaleType = 0
  TheoreticalExact = false
  Type = 2
  UnderTolerance = 0
  X = -79.2211
  Y = 11.4386
FEATURE [TechDraw::DrawViewDimension] Dimension121
  AngleOverride = false
  Arbitrary = false
  ArbitraryTolerances = false
  EqualTolerance = true
  ExtensionAngle = 0
  FormatSpec = ⌀%.2w
  FormatSpecOverTolerance = %+.2w
  FormatSpecUnderTolerance = %+.2w
  Inverted = false
  LineAngle = 0
  LockPosition = false
  MeasureType = 1
  OverTolerance = 0
  References2D = -> [View005]
  Rotation = 0
  Scale = 0.25
  ScaleType = 0
  TheoreticalExact = false
  Type = 5
  UnderTolerance = 0
  X = -61.8915
  Y = -0.615836
FEATURE [TechDraw::DrawViewDimension] Dimension122
  AngleOverride = false
  Arbitrary = false
  ArbitraryTolerances = false
  EqualTolerance = true
  ExtensionAngle = 0
  FormatSpec = ⌀%.2w
  FormatSpecOverTolerance = %+.2w
  FormatSpecUnderTolerance = %+.2w
  Inverted = false
  LineAngle = 0
  LockPosition = false
  MeasureType = 1
  OverTolerance = 0
  References2D = -> [View005]
  Rotation = 0
  Scale = 0.25
  ScaleType = 0
  TheoreticalExact = false
  Type = 5
  UnderTolerance = 0
  X = -34.7947
  Y = 17.1664
FEATURE [TechDraw::DrawPage] Page005  label="vue-percages-tirettes"
  KeepUpdated = true
  NextBalloonIndex = 1
  ProjectionType = 0
  Scale = 0.25
  Template = -> Template005
  Views = -> [View005,Dimension109,Dimension110,Dimension111,Dimension112,Dimension113,Dimension114,Dimension115,Dimension116,Dimension117,Dimension118,Dimension119,Dimension120,Dimension121,Dimension122]
FEATURE [TechDraw::DrawViewDimension] Dimension123
  AngleOverride = false
  Arbitrary = false
  ArbitraryTolerances = false
  EqualTolerance = true
  ExtensionAngle = 0
  FormatSpec = %.2w
  FormatSpecOverTolerance = %+.2w
  FormatSpecUnderTolerance = %+.2w
  Inverted = false
  LineAngle = 0
  LockPosition = false
  MeasureType = 1
  OverTolerance = 0
  References2D = -> [View003]
  Rotation = 0
  ScaleType = 0
  TheoreticalExact = false
  Type = 0
  UnderTolerance = 0
  X = -397.061
  Y = -28.8957
FEATURE [TechDraw::DrawPage] Page003  label="vue-gauche-positions-et-diametres-trous"
  KeepUpdated = true
  NextBalloonIndex = 1
  ProjectionType = 0
  Template = -> Template003
  Views = -> [View003,Dimension026,Dimension028,Dimension030,Dimension031,Dimension032,Dimension033,Dimension034,Dimension037,Dimension039,Dimension040,Dimension041,Dimension042,Dimension043,Dimension044,Dimension049,Dimension056,Dimension057,Dimension059,Dimension060,Dimension061,Dimension062,Dimension063,Dimension064,Dimension065,Dimension066,Dimension067,Dimension068,Dimension069,Dimension070,Dimension071,+10 more]
FEATURE [TechDraw::DrawViewPart] View006  label="Partie gauche"
  CoarseView = false
  Direction = (0,0,1)
  Focus = 100
  HardHidden = false
  IsoCount = 0
  IsoHidden = false
  IsoVisible = false
  LockPosition = false
  Perspective = false
  Rotation = 0
  ScaleType = 0
  SeamHidden = false
  SeamVisible = false
  SmoothHidden = false
  SmoothVisible = false
  Source = -> [Body]
  X = 580
  XDirection = (1,0,0)
  Y = 105
FEATURE [TechDraw::DrawViewBalloon] Balloon003
  BubbleShape = 0
  EndType = 0
  EndTypeScale = 1
  KinkLength = 5
  LockPosition = false
  OriginX = -434.85
  OriginY = 4.5
  Rotation = 0
  ScaleType = 0
  ShapeScale = 1
  SourceView = -> View006
  Text = 1
  TextWrapLen = -1
  X = -414.85
  Y = 24.5
FEATURE [TechDraw::DrawViewBalloon] Balloon004
  BubbleShape = 0
  EndType = 0
  EndTypeScale = 1
  KinkLength = 5
  LockPosition = false
  OriginX = -382.6
  OriginY = -2.7
  Rotation = 0
  ScaleType = 0
  ShapeScale = 1
  SourceView = -> View006
  Text = 2
  TextWrapLen = -1
  X = -399.191
  Y = 13.1637
FEATURE [TechDraw::DrawViewBalloon] Balloon005
  BubbleShape = 0
  EndType = 0
  EndTypeScale = 1
  KinkLength = 5
  LockPosition = false
  OriginX = -399.779
  OriginY = -47.7787
  Rotation = 0
  ScaleType = 0
  ShapeScale = 1
  SourceView = -> View006
  Text = 3
  TextWrapLen = -1
  X = -416.957
  Y = -37.9447
FEATURE [TechDraw::DrawViewBalloon] Balloon006
  BubbleShape = 0
  EndType = 0
  EndTypeScale = 1
  KinkLength = 5
  LockPosition = false
  OriginX = -526.4
  OriginY = -49.9
  Rotation = 0
  ScaleType = 0
  ShapeScale = 1
  SourceView = -> View006
  Text = 4
  TextWrapLen = -1
  X = -508.057
  Y = -39.659
FEATURE [TechDraw::DrawViewBalloon] Balloon007
  BubbleShape = 0
  EndType = 0
  EndTypeScale = 1
  KinkLength = 5
  LockPosition = false
  OriginX = -549
  OriginY = -57
  Rotation = 0
  ScaleType = 0
  ShapeScale = 1
  SourceView = -> View006
  Text = 5
  TextWrapLen = -1
  X = -529
  Y = -37
FEATURE [TechDraw::DrawViewBalloon] Balloon008
  BubbleShape = 0
  EndType = 0
  EndTypeScale = 1
  KinkLength = 5
  LockPosition = false
  OriginX = -549.05
  OriginY = 19
  Rotation = 0
  ScaleType = 0
  ShapeScale = 1
  SourceView = -> View006
  Text = 6
  TextWrapLen = -1
  X = -529.05
  Y = 39
FEATURE [TechDraw::DrawViewAnnotation] Annotation005
  Font = osifont
  LineSpace = 80
  LockPosition = false
  MaxWidth = -1
  Rotation = 0
  ScaleType = 0
  Text = 6 - Fixation panneau acier sur supports bois
  TextSize = 5
  TextStyle = 0
  X = 246.384
  Y = 86.4108
FEATURE [TechDraw::DrawViewBalloon] Balloon009
  BubbleShape = 0
  EndType = 0
  EndTypeScale = 1
  KinkLength = 5
  LockPosition = false
  OriginX = -517.25
  OriginY = 4.5
  Rotation = 0
  ScaleType = 0
  ShapeScale = 1
  SourceView = -> View006
  Text = 1
  TextWrapLen = -1
  X = -497.25
  Y = 24.5
FEATURE [TechDraw::DrawViewBalloon] Balloon010
  BubbleShape = 0
  EndType = 0
  EndTypeScale = 1
  KinkLength = 5
  LockPosition = false
  OriginX = -517.25
  OriginY = -58.9
  Rotation = 0
  ScaleType = 0
  ShapeScale = 1
  SourceView = -> View006
  Text = 1
  TextWrapLen = -1
  X = -499.283
  Y = -70.2693
FEATURE [TechDraw::DrawViewBalloon] Balloon011
  BubbleShape = 0
  EndType = 0
  EndTypeScale = 1
  KinkLength = 5
  LockPosition = false
  OriginX = -434.85
  OriginY = -58.9
  Rotation = 0
  ScaleType = 0
  ShapeScale = 1
  SourceView = -> View006
  Text = 1
  TextWrapLen = -1
  X = -418.916
  Y = -70.8502
FEATURE [TechDraw::DrawViewBalloon] Balloon012
  BubbleShape = 0
  EndType = 0
  EndTypeScale = 1
  KinkLength = 5
  LockPosition = false
  OriginX = -382.6
  OriginY = 69
  Rotation = 0
  ScaleType = 0
  ShapeScale = 1
  SourceView = -> View006
  Text = 2
  TextWrapLen = -1
  X = -400.359
  Y = 62.5685
FEATURE [TechDraw::DrawViewBalloon] Balloon013
  BubbleShape = 0
  EndType = 0
  EndTypeScale = 1
  KinkLength = 5
  LockPosition = false
  OriginX = -547.5
  OriginY = -9
  Rotation = 0
  ScaleType = 0
  ShapeScale = 1
  SourceView = -> View006
  Text = 7
  TextWrapLen = -1
  X = -524.015
  Y = -12.527
FEATURE [TechDraw::DrawViewBalloon] Balloon014
  BubbleShape = 0
  EndType = 0
  EndTypeScale = 1
  KinkLength = 5
  LockPosition = false
  OriginX = -470.5
  OriginY = 30
  Rotation = 0
  ScaleType = 0
  ShapeScale = 1
  SourceView = -> View006
  Text = 7
  TextWrapLen = -1
  X = -446.724
  Y = 38.0913
FEATURE [TechDraw::DrawViewAnnotation] Annotation006
  Font = osifont
  LineSpace = 80
  LockPosition = false
  MaxWidth = -1
  Rotation = 0
  ScaleType = 0
  Text = 7 - Fixation bloc latéral bois
  TextSize = 5
  TextStyle = 0
  X = 229.537
  Y = 61.722
FEATURE [TechDraw::DrawPage] Page006  label="nomenclature-percages-gauche"
  KeepUpdated = true
  NextBalloonIndex = 13
  ProjectionType = 0
  Template = -> Template006
  Views = -> [View006,Annotation,Balloon003,Balloon004,Annotation001,Balloon005,Annotation002,Balloon006,Annotation003,Balloon007,Annotation004,Balloon008,Annotation005,Balloon009,Balloon010,Balloon011,Balloon012,Balloon013,Balloon014,Annotation006]
FEATURE [TechDraw::DrawSVGTemplate] Template007
  Height = 210
  Orientation = 1
  Width = 297
FEATURE [TechDraw::DrawViewPart] View007
  CoarseView = false
  Direction = (0,0,1)
  Focus = 100
  HardHidden = false
  IsoCount = 0
  IsoHidden = false
  IsoVisible = false
  LockPosition = false
  Perspective = false
  Rotation = 0
  ScaleType = 0
  SeamHidden = false
  SeamVisible = false
  SmoothHidden = false
  SmoothVisible = false
  Source = -> [Body]
  X = -285.5
  XDirection = (1,0,0)
  Y = 105
FEATURE [TechDraw::DrawViewBalloon] Balloon015
  BubbleShape = 0
  EndType = 0
  EndTypeScale = 1
  KinkLength = 5
  LockPosition = false
  OriginX = 512.65
  OriginY = 4.5
  Rotation = 0
  ScaleType = 0
  ShapeScale = 1
  SourceView = -> View007
  Text = 1
  TextWrapLen = -1
  X = 494.019
  Y = 15.4959
FEATURE [TechDraw::DrawViewBalloon] Balloon016
  BubbleShape = 0
  EndType = 0
  EndTypeScale = 1
  KinkLength = 5
  LockPosition = false
  OriginX = 381.45
  OriginY = 4.5
  Rotation = 0
  ScaleType = 0
  ShapeScale = 1
  SourceView = -> View007
  Text = 1
  TextWrapLen = -1
  X = 359.334
  Y = 12.5913
FEATURE [TechDraw::DrawViewBalloon] Balloon017
  BubbleShape = 0
  EndType = 0
  EndTypeScale = 1
  KinkLength = 5
  LockPosition = false
  OriginX = 381.45
  OriginY = -58.9
  Rotation = 0
  ScaleType = 0
  ShapeScale = 1
  SourceView = -> View007
  Text = 1
  TextWrapLen = -1
  X = 365.433
  Y = -65.3315
FEATURE [TechDraw::DrawViewBalloon] Balloon018
  BubbleShape = 0
  EndType = 0
  EndTypeScale = 1
  KinkLength = 5
  LockPosition = false
  OriginX = 512.65
  OriginY = -58.9
  Rotation = 0
  ScaleType = 0
  ShapeScale = 1
  SourceView = -> View007
  Text = 1
  TextWrapLen = -1
  X = 494.019
  Y = -66.7838
FEATURE [TechDraw::DrawViewBalloon] Balloon019
  BubbleShape = 0
  EndType = 0
  EndTypeScale = 1
  KinkLength = 5
  LockPosition = false
  OriginX = 379.2
  OriginY = 69
  Rotation = 0
  ScaleType = 0
  ShapeScale = 1
  SourceView = -> View007
  Text = 2
  TextWrapLen = -1
  X = 359.988
  Y = 56.7593
FEATURE [TechDraw::DrawViewBalloon] Balloon020
  BubbleShape = 0
  EndType = 0
  EndTypeScale = 1
  KinkLength = 5
  LockPosition = false
  OriginX = 379.2
  OriginY = -2.7
  Rotation = 0
  ScaleType = 0
  ShapeScale = 1
  SourceView = -> View007
  Text = 2
  TextWrapLen = -1
  X = 359.407
  Y = -10.2934
FEATURE [TechDraw::DrawViewBalloon] Balloon021
  BubbleShape = 0
  EndType = 0
  EndTypeScale = 1
  KinkLength = 5
  LockPosition = false
  OriginX = 384.1
  OriginY = -49.9
  Rotation = 0
  ScaleType = 0
  ShapeScale = 1
  SourceView = -> View007
  Text = 4
  TextWrapLen = -1
  X = 365.179
  Y = -40.9373
FEATURE [TechDraw::DrawViewBalloon] Balloon022
  BubbleShape = 0
  EndType = 0
  EndTypeScale = 1
  KinkLength = 5
  LockPosition = false
  OriginX = 523.1
  OriginY = -49.9
  Rotation = 0
  ScaleType = 0
  ShapeScale = 1
  SourceView = -> View007
  Text = 4
  TextWrapLen = -1
  X = 543.1
  Y = -29.9
FEATURE [TechDraw::DrawViewBalloon] Balloon023
  BubbleShape = 0
  EndType = 0
  EndTypeScale = 1
  KinkLength = 5
  LockPosition = false
  OriginX = 543
  OriginY = -57
  Rotation = 0
  ScaleType = 0
  ShapeScale = 1
  SourceView = -> View007
  Text = 5
  TextWrapLen = -1
  X = 527.564
  Y = -67.7884
FEATURE [TechDraw::DrawViewBalloon] Balloon024
  BubbleShape = 0
  EndType = 0
  EndTypeScale = 1
  KinkLength = 5
  LockPosition = false
  OriginX = 542.95
  OriginY = 19
  Rotation = 0
  ScaleType = 0
  ShapeScale = 1
  SourceView = -> View007
  Text = 6
  TextWrapLen = -1
  X = 522.286
  Y = 31.7386
FEATURE [TechDraw::DrawViewBalloon] Balloon025
  BubbleShape = 0
  EndType = 0
  EndTypeScale = 1
  KinkLength = 5
  LockPosition = false
  OriginX = 544.5
  OriginY = -9
  Rotation = 0
  ScaleType = 0
  ShapeScale = 1
  SourceView = -> View007
  Text = 7
  TextWrapLen = -1
  X = 518.898
  Y = -15.722
FEATURE [TechDraw::DrawViewBalloon] Balloon026
  BubbleShape = 0
  EndType = 0
  EndTypeScale = 1
  KinkLength = 5
  LockPosition = false
  OriginX = 467.5
  OriginY = 30
  Rotation = 0
  ScaleType = 0
  ShapeScale = 1
  SourceView = -> View007
  Text = 7
  TextWrapLen = -1
  X = 487.5
  Y = 50
FEATURE [TechDraw::DrawPage] Page007  label="nomenclature-percages-droite"
  KeepUpdated = true
  NextBalloonIndex = 13
  ProjectionType = 0
  Template = -> Template007
  Views = -> [View007,Balloon015,Balloon016,Balloon017,Balloon018,Balloon019,Balloon020,Balloon021,Balloon022,Balloon023,Balloon024,Balloon025,Balloon026]
